# Revit family: CAF_DWDI_CW_UBD
name_source: partatom
category: Mechanical Equipment
units: mm (PartAtom-declared; Revit-internal decimal feet)

## family parameters
Always vertical = Yes
Cut with Voids When Loaded = No
Part Type = Normal
Room Calculation Point = No
Round Connector Dimension = Use Radius
Shared = No
Work Plane-Based = No

## types (58) — shared parameters
0 = 0"
1" = 1"
1.5 = 1 1/2"
2" = 2"
2' = 24"
3" = 3"
60 = 60.00°
Manufacturer = Loren Cook Company
Model = CAF-DWDI
ONE EIGTH = 1/8"
URL = www.lorencook.com

## per-type parameters (varying)
- 120_CAF-DWDI_CW_UBD_CLASS_1: ((M+U+U+N+N)-((B+.25")/2))/2=3"; (A+.25")/2=6 3/16"; (B+.25")/2=8 31/32"; (D-(A+.25"))/2=15/16"; (INLET/2)+1.5"=9 1/2"; (INLET/2)+1.625"=9 9/16"; (INLET/2)-.125"=7 15/16"; (M-(B+.25")/2=1 7/16"; -(B+.25")/2=-8 31/32"; -P=-26 11/16"; A=12 1/8"; A+.25"=12 3/8"; A/2=6 1/16"; B=17 11/16"; B+.25"=17 15/16"; B/2=8 27/32"; BOTTOM=9 5/8"; C=1 7/16"; C+C=2 7/8"; C/2=23/32"; D=14 1/4"; D/2=7 1/8"; D/7=1 1/2"; E=19 13/16"; E/2=9 29/32"; F=21 1/16"; F-((D-A-.25")/2)=20 1/8"; G=11 7/16"; G+(INLET/2)+1.625"=21"; G-(INLET/2)-1.625"=1 7/8"; G-(R/2)=1 13/16"; H=23 1/16"; H-((D-A-.25")/2)=22 1/8"; H-J=13 13/16"; INLET=16 1/8"; INLET/2=8 1/16"; INLET/4=4 1/32"; J=9 1/4"; K=9/16"; K/2=9/32"; L=10 7/16"; M=20 13/16"; N=2 3/4"; P=26 11/16"; R=19 1/4"; R/2=9 5/8"; S=14 7/8"; S/2=7 7/16"; SCROLL2=9"; T=19 7/16"; T/2=9 23/32"; Type Comments=Centrifugal Airfoil Blower Clockwise Up Blast Arrangement 3 Low Profile Class 1; U=4 5/16"; U-N=1 9/16"; V=1"; V+(D-(A+.25"))/2=1 15/16"
- 135_CAF-DWDI_CW_UBD_CLASS_1: ((M+U+U+N+N)-((B+.25")/2))/2=3"; (A+.25")/2=6 15/16"; (B+.25")/2=10 3/32"; (D-(A+.25"))/2=15/16"; (INLET/2)+1.5"=10 1/4"; (INLET/2)+1.625"=10 5/16"; (INLET/2)-.125"=8 11/16"; (M-(B+.25")/2=1 7/16"; -(B+.25")/2=-10 3/32"; -P=-28 15/16"; A=13 5/8"; A+.25"=13 7/8"; A/2=6 13/16"; B=19 15/16"; B+.25"=20 3/16"; B/2=9 31/32"; BOTTOM=10 13/16"; C=1 7/16"; C+C=2 7/8"; C/2=23/32"; D=15 3/4"; D/2=7 7/8"; D/7=1 21/32"; E=22 1/16"; E/2=11 1/32"; F=23 9/16"; F-((D-A-.25")/2)=22 5/8"; G=12 3/4"; G+(INLET/2)+1.625"=23 1/16"; G-(INLET/2)-1.625"=2 7/16"; G-(R/2)=2 1/4"; H=25 3/4"; H-((D-A-.25")/2)=24 13/16"; H-J=15 3/8"; INLET=17 5/8"; INLET/2=8 13/16"; INLET/4=4 13/32"; J=10 3/8"; K=9/16"; K/2=9/32"; L=11 9/16"; M=23 1/16"; N=2 3/4"; P=28 15/16"; R=21"; R/2=10 1/2"; S=16 5/8"; S/2=8 5/16"; SCROLL2=10 1/2"; T=21 3/4"; T/2=10 7/8"; Type Comments=Centrifugal Airfoil Blower Clockwise Up Blast Arrangement 3 Low Profile Class 1; U=4 5/16"; U-N=1 9/16"; V=1"; V+(D-(A+.25"))/2=1 15/16"
- 150_CAF-DWDI_CW_UBD_CLASS_1: ((M+U+U+N+N)-((B+.25")/2))/2=3"; (A+.25")/2=7 3/4"; (B+.25")/2=11 1/8"; (D-(A+.25"))/2=15/16"; (INLET/2)+1.5"=11"; (INLET/2)+1.625"=11 1/16"; (INLET/2)-.125"=9 7/16"; (M-(B+.25")/2=1 15/16"; -(B+.25")/2=-11 1/8"; -P=-31 5/8"; A=15 1/4"; A+.25"=15 1/2"; A/2=7 5/8"; B=22"; B+.25"=22 1/4"; B/2=11"; BOTTOM=12"; C=1 7/16"; C+C=2 7/8"; C/2=23/32"; D=17 3/8"; D/2=8 11/16"; D/7=1 27/32"; E=24 1/8"; E/2=12 1/16"; F=26 1/16"; F-((D-A-.25")/2)=25 1/8"; G=14 1/16"; G+(INLET/2)+1.625"=25 1/8"; G-(INLET/2)-1.625"=3"; G-(R/2)=2 13/16"; H=28 7/16"; H-((D-A-.25")/2)=27 1/2"; H-J=16 15/16"; INLET=19 1/8"; INLET/2=9 9/16"; INLET/4=4 25/32"; J=11 1/2"; K=9/16"; K/2=9/32"; L=13 1/16"; M=26 1/8"; N=3 3/8"; P=31 5/8"; R=22 1/2"; R/2=11 1/4"; S=17 3/4"; S/2=8 7/8"; SCROLL2=11 1/4"; T=24 3/8"; T/2=12 3/16"; Type Comments=Centrifugal Airfoil Blower Clockwise Up Blast Arrangement 3 Low Profile Class 1; U=4 7/16"; U-N=1 1/16"; V=1"; V+(D-(A+.25"))/2=1 15/16"
- 165_CAF-DWDI_CW_UBD_CLASS_1: ((M+U+U+N+N)-((B+.25")/2))/2=3"; (A+.25")/2=8 19/32"; (B+.25")/2=12 1/8"; (D-(A+.25"))/2=15/16"; (INLET/2)+1.5"=12 1/32"; (INLET/2)+1.625"=12 3/32"; (INLET/2)-.125"=10 15/32"; (M-(B+.25")/2=1 15/16"; -(B+.25")/2=-12 1/8"; -P=-33 11/16"; A=16 15/16"; A+.25"=17 3/16"; A/2=8 15/32"; B=24"; B+.25"=24 1/4"; B/2=12"; BOTTOM=13 1/8"; C=1 11/16"; C+C=3 3/8"; C/2=27/32"; D=19 1/16"; D/2=9 17/32"; D/7=2"; E=26 1/8"; E/2=13 1/16"; F=28 1/2"; F-((D-A-.25")/2)=27 9/16"; G=15 3/8"; G+(INLET/2)+1.625"=27 15/32"; G-(INLET/2)-1.625"=3 9/32"; G-(R/2)=3 1/4"; H=31 3/16"; H-((D-A-.25")/2)=30 1/4"; H-J=18 1/2"; INLET=21 3/16"; INLET/2=10 19/32"; INLET/4=5 5/16"; J=12 11/16"; K=15/16"; K/2=15/32"; L=14 1/16"; M=28 1/8"; N=3 3/8"; P=33 11/16"; R=24 1/4"; R/2=12 1/8"; S=19 1/2"; S/2=9 3/4"; SCROLL2=12 1/8"; T=26 3/8"; T/2=13 3/16"; Type Comments=Centrifugal Airfoil Blower Clockwise Up Blast Arrangement 3 Low Profile Class 1; U=4 7/16"; U-N=1 1/16"; V=1"; V+(D-(A+.25"))/2=1 15/16"
- 180_CAF-DWDI_CW_UBD_CLASS_1: ((M+U+U+N+N)-((B+.25")/2))/2=3"; (A+.25")/2=9 3/8"; (B+.25")/2=13 5/32"; (D-(A+.25"))/2=15/16"; (INLET/2)+1.5"=12 25/32"; (INLET/2)+1.625"=12 27/32"; (INLET/2)-.125"=11 7/32"; (M-(B+.25")/2=1 15/16"; -(B+.25")/2=-13 5/32"; -P=-36 1/8"; A=18 1/2"; A+.25"=18 3/4"; A/2=9 1/4"; B=26 1/16"; B+.25"=26 5/16"; B/2=13 1/32"; BOTTOM=14 5/16"; C=1 11/16"; C+C=3 3/8"; C/2=27/32"; D=20 5/8"; D/2=10 5/16"; D/7=2 5/32"; E=28 3/16"; E/2=14 3/32"; F=31"; F-((D-A-.25")/2)=30 1/16"; G=16 11/16"; G+(INLET/2)+1.625"=29 17/32"; G-(INLET/2)-1.625"=3 27/32"; G-(R/2)=3 5/16"; H=34"; H-((D-A-.25")/2)=33 1/16"; H-J=20 3/16"; INLET=22 11/16"; INLET/2=11 11/32"; INLET/4=5 11/16"; J=13 13/16"; K=15/16"; K/2=15/32"; L=15 1/8"; M=30 3/16"; N=3 3/4"; P=36 1/8"; R=26 3/4"; R/2=13 3/8"; S=21"; S/2=10 1/2"; SCROLL2=13 3/8"; T=28 7/16"; T/2=14 7/32"; Type Comments=Centrifugal Airfoil Blower Clockwise Up Blast Arrangement 3 Low Profile Class 1; U=4 13/16"; U-N=1 1/16"; V=1"; V+(D-(A+.25"))/2=1 15/16"
- 195_CAF-DWDI_CW_UBD_CLASS_1: ((M+U+U+N+N)-((B+.25")/2))/2=3"; (A+.25")/2=9 7/8"; (B+.25")/2=14 11/32"; (D-(A+.25"))/2=31/32"; (INLET/2)+1.5"=13 17/32"; (INLET/2)+1.625"=13 19/32"; (INLET/2)-.125"=11 31/32"; (M-(B+.25")/2=1 15/16"; -(B+.25")/2=-14 11/32"; -P=-38 1/2"; A=19 1/2"; A+.25"=19 3/4"; A/2=9 3/4"; B=28 7/16"; B+.25"=28 11/16"; B/2=14 7/32"; BOTTOM=15 1/2"; C=1 11/16"; C+C=3 3/8"; C/2=27/32"; D=21 11/16"; D/2=10 27/32"; D/7=2 9/32"; E=30 5/8"; E/2=15 5/16"; F=33 7/16"; F-((D-A-.25")/2)=32 15/32"; G=17 15/16"; G+(INLET/2)+1.625"=31 17/32"; G-(INLET/2)-1.625"=4 11/32"; G-(R/2)=3 11/16"; H=36 11/16"; H-((D-A-.25")/2)=35 23/32"; H-J=21 3/4"; INLET=24 3/16"; INLET/2=12 3/32"; INLET/4=6 1/16"; J=14 15/16"; K=15/16"; K/2=15/32"; L=16 5/16"; M=32 9/16"; N=3 3/4"; P=38 1/2"; R=28 1/2"; R/2=14 1/4"; S=22 3/4"; S/2=11 3/8"; SCROLL2=14 1/4"; T=30 13/16"; T/2=15 13/32"; Type Comments=Centrifugal Airfoil Blower Clockwise Up Blast Arrangement 3 Low Profile Class 1; U=4 13/16"; U-N=1 1/16"; V=1"; V+(D-(A+.25"))/2=1 31/32"
- 210_CAF-DWDI_CW_UBD_CLASS_1: ((M+U+U+N+N)-((B+.25")/2))/2=4"; (A+.25")/2=10 15/16"; (B+.25")/2=15 5/16"; (D-(A+.25"))/2=31/32"; (INLET/2)+1.5"=14 13/32"; (INLET/2)+1.625"=14 15/32"; (INLET/2)-.125"=12 27/32"; (M-(B+.25")/2=1 15/16"; -(B+.25")/2=-15 5/16"; -P=-41 7/16"; A=21 5/8"; A+.25"=21 7/8"; A/2=10 13/16"; B=30 3/8"; B+.25"=30 5/8"; B/2=15 3/16"; BOTTOM=16 11/16"; C=1 11/16"; C+C=3 3/8"; C/2=27/32"; D=23 13/16"; D/2=11 29/32"; D/7=2 1/2"; E=32 9/16"; E/2=16 9/32"; F=35 15/16"; F-((D-A-.25")/2)=34 31/32"; G=19 1/4"; G+(INLET/2)+1.625"=33 23/32"; G-(INLET/2)-1.625"=4 25/32"; G-(R/2)=4 1/4"; H=39 7/16"; H-((D-A-.25")/2)=38 15/32"; H-J=23 5/16"; INLET=25 15/16"; INLET/2=12 31/32"; INLET/4=6 1/2"; J=16 1/8"; K=15/16"; K/2=15/32"; L=17 1/4"; M=34 1/2"; N=3 3/4"; P=41 7/16"; R=30"; R/2=15"; S=24 1/4"; S/2=12 1/8"; SCROLL2=15"; T=32 3/4"; T/2=16 3/8"; Type Comments=Centrifugal Airfoil Blower Clockwise Up Blast Arrangement 3 Low Profile Class 1; U=5 13/16"; U-N=2 1/16"; V=1"; V+(D-(A+.25"))/2=1 31/32"
- 225_CAF-DWDI_CW_UBD_CLASS_1: ((M+U+U+N+N)-((B+.25")/2))/2=4"; (A+.25")/2=11 23/32"; (B+.25")/2=16 3/8"; (D-(A+.25"))/2=1 15/32"; (INLET/2)+1.5"=15 5/32"; (INLET/2)+1.625"=15 7/32"; (INLET/2)-.125"=13 19/32"; (M-(B+.25")/2=1 15/16"; -(B+.25")/2=-16 3/8"; -P=-44 1/16"; A=23 3/16"; A+.25"=23 7/16"; A/2=11 19/32"; B=32 1/2"; B+.25"=32 3/4"; B/2=16 1/4"; BOTTOM=17 13/16"; C=1 15/16"; C+C=3 7/8"; C/2=31/32"; D=26 3/8"; D/2=13 3/16"; D/7=2 25/32"; E=35 11/16"; E/2=17 27/32"; F=38 3/8"; F-((D-A-.25")/2)=36 29/32"; G=20 9/16"; G+(INLET/2)+1.625"=35 25/32"; G-(INLET/2)-1.625"=5 11/32"; G-(R/2)=4 11/16"; H=42 11/16"; H-((D-A-.25")/2)=41 7/32"; H-J=25 7/16"; INLET=27 7/16"; INLET/2=13 23/32"; INLET/4=6 7/8"; J=17 1/4"; K=15/16"; K/2=15/32"; L=18 5/16"; M=36 5/8"; N=4 1/4"; P=44 1/16"; R=31 3/4"; R/2=15 7/8"; S=26"; S/2=13"; SCROLL2=15 7/8"; T=34 7/8"; T/2=17 7/16"; Type Comments=Centrifugal Airfoil Blower Clockwise Up Blast Arrangement 3 Low Profile Class 1; U=6 5/16"; U-N=2 1/16"; V=1"; V+(D-(A+.25"))/2=2 15/32"
- 245_CAF-DWDI_CW_UBD_CLASS_1: ((M+U+U+N+N)-((B+.25")/2))/2=4"; (A+.25")/2=12 7/8"; (B+.25")/2=17 21/32"; (D-(A+.25"))/2=1 15/32"; (INLET/2)+1.5"=16 5/32"; (INLET/2)+1.625"=16 7/32"; (INLET/2)-.125"=14 19/32"; (M-(B+.25")/2=1 15/16"; -(B+.25")/2=-17 21/32"; -P=-46 5/8"; A=25 1/2"; A+.25"=25 3/4"; A/2=12 3/4"; B=35 1/16"; B+.25"=35 5/16"; B/2=17 17/32"; BOTTOM=19 3/8"; C=1 15/16"; C+C=3 7/8"; C/2=31/32"; D=28 11/16"; D/2=14 11/32"; D/7=3 1/32"; E=38 1/4"; E/2=19 1/8"; F=41 11/16"; F-((D-A-.25")/2)=40 7/32"; G=22 5/16"; G+(INLET/2)+1.625"=38 17/32"; G-(INLET/2)-1.625"=6 3/32"; G-(R/2)=5 7/16"; H=46 5/16"; H-((D-A-.25")/2)=44 27/32"; H-J=27 9/16"; INLET=29 7/16"; INLET/2=14 23/32"; INLET/4=7 3/8"; J=18 3/4"; K=15/16"; K/2=15/32"; L=19 5/8"; M=39 3/16"; N=4 1/4"; P=46 5/8"; R=33 3/4"; R/2=16 7/8"; S=28"; S/2=14"; SCROLL2=16 7/8"; T=37 7/16"; T/2=18 23/32"; Type Comments=Centrifugal Airfoil Blower Clockwise Up Blast Arrangement 3 Low Profile Class 1; U=6 5/16"; U-N=2 1/16"; V=1"; V+(D-(A+.25"))/2=2 15/32"
- 270_CAF-DWDI_CW_UBD_CLASS_1: ((M+U+U+N+N)-((B+.25")/2))/2=4 1/2"; (A+.25")/2=13 7/8"; (B+.25")/2=19 27/32"; (D-(A+.25"))/2=1 15/32"; (INLET/2)+1.5"=17 13/32"; (INLET/2)+1.625"=17 15/32"; (INLET/2)-.125"=15 27/32"; (M-(B+.25")/2=2 7/16"; -(B+.25")/2=-19 27/32"; -P=-51 1/2"; A=27 1/2"; A+.25"=27 3/4"; A/2=13 3/4"; B=39 7/16"; B+.25"=39 11/16"; B/2=19 23/32"; BOTTOM=21 5/16"; C=2 3/16"; C+C=4 3/8"; C/2=1 3/32"; D=30 11/16"; D/2=15 11/32"; D/7=3 7/32"; E=42 5/8"; E/2=21 5/16"; F=45 13/16"; F-((D-A-.25")/2)=44 11/32"; G=24 1/2"; G+(INLET/2)+1.625"=41 31/32"; G-(INLET/2)-1.625"=7 1/32"; G-(R/2)=5 3/4"; H=50 7/8"; H-((D-A-.25")/2)=49 13/32"; H-J=30 3/16"; INLET=31 15/16"; INLET/2=15 31/32"; INLET/4=8"; J=20 11/16"; K=15/16"; K/2=15/32"; L=22 5/16"; M=44 9/16"; N=4 1/4"; P=51 1/2"; R=37 1/2"; R/2=18 3/4"; S=30 1/4"; S/2=15 1/8"; SCROLL2=18 3/4"; T=42 5/16"; T/2=21 5/32"; Type Comments=Centrifugal Airfoil Blower Clockwise Up Blast Arrangement 3 Low Profile Class 1; U=6 5/16"; U-N=2 1/16"; V=1"; V+(D-(A+.25"))/2=2 15/32"
- 300_CAF-DWDI_CW_UBD_CLASS_1: ((M+U+U+N+N)-((B+.25")/2))/2=4 9/16"; (A+.25")/2=15 23/32"; (B+.25")/2=21 5/8"; (D-(A+.25"))/2=1 15/32"; (INLET/2)+1.5"=18 29/32"; (INLET/2)+1.625"=18 31/32"; (INLET/2)-.125"=17 11/32"; (M-(B+.25")/2=2 7/16"; -(B+.25")/2=-21 5/8"; -P=-55 1/8"; A=31 3/16"; A+.25"=31 7/16"; A/2=15 19/32"; B=43"; B+.25"=43 1/4"; B/2=21 1/2"; BOTTOM=23 11/16"; C=2 3/16"; C+C=4 3/8"; C/2=1 3/32"; D=34 3/8"; D/2=17 3/16"; D/7=3 5/8"; E=46 3/16"; E/2=23 3/32"; F=50 3/4"; F-((D-A-.25")/2)=49 9/32"; G=27 1/16"; G+(INLET/2)+1.625"=46 1/32"; G-(INLET/2)-1.625"=8 3/32"; G-(R/2)=6 13/16"; H=56 5/16"; H-((D-A-.25")/2)=54 27/32"; H-J=33 3/8"; INLET=34 15/16"; INLET/2=17 15/32"; INLET/4=8 3/4"; J=22 15/16"; K=15/16"; K/2=15/32"; L=24 1/16"; M=48 1/8"; N=4 1/4"; P=55 1/8"; R=40 1/2"; R/2=20 1/4"; S=33 1/4"; S/2=16 5/8"; SCROLL2=20 1/4"; T=45 7/8"; T/2=22 15/16"; Type Comments=Centrifugal Airfoil Blower Clockwise Up Blast Arrangement 3 Low Profile Class 1; U=6 3/8"; U-N=2 1/8"; V=1"; V+(D-(A+.25"))/2=2 15/32"
- 330_CAF-DWDI_CW_UBD_CLASS_1: ((M+U+U+N+N)-((B+.25")/2))/2=4 9/16"; (A+.25")/2=17 3/8"; (B+.25")/2=23 21/32"; (D-(A+.25"))/2=2"; (INLET/2)+1.5"=20 13/32"; (INLET/2)+1.625"=20 15/32"; (INLET/2)-.125"=18 27/32"; (M-(B+.25")/2=2 15/16"; -(B+.25")/2=-23 21/32"; -P=-59 5/16"; A=34 1/2"; A+.25"=34 3/4"; A/2=17 1/4"; B=47 1/16"; B+.25"=47 5/16"; B/2=23 17/32"; BOTTOM=26"; C=2 7/16"; C+C=4 7/8"; C/2=1 7/32"; D=38 3/4"; D/2=19 3/8"; D/7=4 3/32"; E=51 5/16"; E/2=25 21/32"; F=55 11/16"; F-((D-A-.25")/2)=53 11/16"; G=29 11/16"; G+(INLET/2)+1.625"=50 5/32"; G-(INLET/2)-1.625"=9 7/32"; G-(R/2)=8 29/32"; H=62 5/16"; H-((D-A-.25")/2)=60 5/16"; H-J=37 1/16"; INLET=37 15/16"; INLET/2=18 31/32"; INLET/4=9 1/2"; J=25 1/4"; K=15/16"; K/2=15/32"; L=26 5/8"; M=53 3/16"; N=4 3/8"; P=59 5/16"; R=41 9/16"; R/2=20 25/32"; S=36 1/8"; S/2=18 1/16"; SCROLL2=20 25/32"; T=50 9/16"; T/2=25 9/32"; Type Comments=Centrifugal Airfoil Blower Clockwise Up Blast Arrangement 3 Low Profile Class 1; U=6"; U-N=1 5/8"; V=1"; V+(D-(A+.25"))/2=3"
- 365_CAF-DWDI_CW_UBD_CLASS_1: ((M+U+U+N+N)-((B+.25")/2))/2=5 1/16"; (A+.25")/2=19 15/32"; (B+.25")/2=26 7/32"; (D-(A+.25"))/2=2"; (INLET/2)+1.5"=22 5/32"; (INLET/2)+1.625"=22 7/32"; (INLET/2)-.125"=20 19/32"; (M-(B+.25")/2=2 15/16"; -(B+.25")/2=-26 7/32"; -P=-65 5/16"; A=38 11/16"; A+.25"=38 15/16"; A/2=19 11/32"; B=52 3/16"; B+.25"=52 7/16"; B/2=26 3/32"; BOTTOM=28 3/4"; C=2 11/16"; C+C=5 3/8"; C/2=1 11/32"; D=42 15/16"; D/2=21 15/32"; D/7=4 17/32"; E=56 7/16"; E/2=28 7/32"; F=61 1/2"; F-((D-A-.25")/2)=59 1/2"; G=32 3/4"; G+(INLET/2)+1.625"=54 31/32"; G-(INLET/2)-1.625"=10 17/32"; G-(R/2)=10 3/32"; H=68 11/16"; H-((D-A-.25")/2)=66 11/16"; H-J=40 3/4"; INLET=41 7/16"; INLET/2=20 23/32"; INLET/4=10 3/8"; J=27 15/16"; K=15/16"; K/2=15/32"; L=29 3/16"; M=58 5/16"; N=4 3/4"; P=65 5/16"; R=45 5/16"; R/2=22 21/32"; S=39 7/8"; S/2=19 15/16"; SCROLL2=22 21/32"; T=55 11/16"; T/2=27 27/32"; Type Comments=Centrifugal Airfoil Blower Clockwise Up Blast Arrangement 3 Low Profile Class 1; U=6 7/8"; U-N=2 1/8"; V=1"; V+(D-(A+.25"))/2=3"
- 402_CAF-DWDI_CW_UBD_CLASS_1: ((M+U+U+N+N)-((B+.25")/2))/2=5 1/16"; (A+.25")/2=21"; (B+.25")/2=29 1/32"; (D-(A+.25"))/2=2 1/32"; (INLET/2)+1.5"=24 1/32"; (INLET/2)+1.625"=24 3/32"; (INLET/2)-.125"=22 15/32"; (M-(B+.25")/2=3 15/16"; -(B+.25")/2=-29 1/32"; -P=-71 15/16"; A=41 3/4"; A+.25"=42"; A/2=20 7/8"; B=57 13/16"; B+.25"=58 1/16"; B/2=28 29/32"; BOTTOM=31 11/16"; C=2 15/16"; C+C=5 7/8"; C/2=1 15/32"; D=46 1/16"; D/2=23 1/32"; D/7=4 27/32"; E=62"; E/2=31"; F=67 5/8"; F-((D-A-.25")/2)=65 19/32"; G=35 15/16"; G+(INLET/2)+1.625"=60 1/32"; G-(INLET/2)-1.625"=11 27/32"; G-(R/2)=11 3/32"; H=75 7/16"; H-((D-A-.25")/2)=73 13/32"; H-J=44 11/16"; INLET=45 3/16"; INLET/2=22 19/32"; INLET/4=11 5/16"; J=30 3/4"; K=15/16"; K/2=15/32"; L=33"; M=65 15/16"; N=4 7/8"; P=71 15/16"; R=49 11/16"; R/2=24 27/32"; S=43"; S/2=21 1/2"; SCROLL2=24 27/32"; T=62 7/16"; T/2=31 7/32"; Type Comments=Centrifugal Airfoil Blower Clockwise Up Blast Arrangement 3 Low Profile Class 1; U=6"; U-N=1 1/8"; V=1 15/16"; V+(D-(A+.25"))/2=3 31/32"
- 445_CAF-DWDI_CW_UBD_CLASS_1: ((M+U+U+N+N)-((B+.25")/2))/2=5 3/32"; (A+.25")/2=23 3/32"; (B+.25")/2=32 1/4"; (D-(A+.25"))/2=2 1/16"; (INLET/2)+1.5"=26 5/32"; (INLET/2)+1.625"=26 7/32"; (INLET/2)-.125"=24 19/32"; (M-(B+.25")/2=3 31/32"; -(B+.25")/2=-32 1/4"; -P=-79 5/16"; A=45 15/16"; A+.25"=46 3/16"; A/2=22 31/32"; B=64 1/4"; B+.25"=64 1/2"; B/2=32 1/8"; BOTTOM=35"; C=2 15/16"; C+C=5 7/8"; C/2=1 15/32"; D=50 5/16"; D/2=25 5/32"; D/7=5 9/32"; E=68 9/16"; E/2=34 9/32"; F=74 11/16"; F-((D-A-.25")/2)=72 5/8"; G=39 11/16"; G+(INLET/2)+1.625"=65 29/32"; G-(INLET/2)-1.625"=13 15/32"; G-(R/2)=12 23/32"; H=83 5/16"; H-((D-A-.25")/2)=81 1/4"; H-J=49 1/4"; INLET=49 7/16"; INLET/2=24 23/32"; INLET/4=12 3/8"; J=34 1/16"; K=1 1/16"; K/2=17/32"; L=36 1/4"; M=72 7/16"; N=5 3/4"; P=79 5/16"; R=53 15/16"; R/2=26 31/32"; S=47 1/4"; S/2=23 5/8"; SCROLL2=26 31/32"; T=68 15/16"; T/2=34 15/32"; Type Comments=Centrifugal Airfoil Blower Clockwise Up Blast Arrangement 3 Low Profile Class 1; U=6 7/8"; U-N=1 1/8"; V=1 15/16"; V+(D-(A+.25"))/2=4"
- 490_CAF-DWDI_CW_UBD_CLASS_1: ((M+U+U+N+N)-((B+.25")/2))/2=5 3/32"; (A+.25")/2=25 5/8"; (B+.25")/2=35 3/16"; (D-(A+.25"))/2=2 1/16"; (INLET/2)+1.5"=28 15/16"; (INLET/2)+1.625"=29"; (INLET/2)-.125"=27 3/8"; (M-(B+.25")/2=3 31/32"; -(B+.25")/2=-35 3/16"; -P=-85 5/16"; A=51"; A+.25"=51 1/4"; A/2=25 1/2"; B=70 1/8"; B+.25"=70 3/8"; B/2=35 1/16"; BOTTOM=38 9/16"; C=3 7/16"; C+C=6 7/8"; C/2=1 23/32"; D=55 3/8"; D/2=27 11/16"; D/7=5 27/32"; E=74 7/16"; E/2=37 7/32"; F=82 1/8"; F-((D-A-.25")/2)=80 1/16"; G=43 9/16"; G+(INLET/2)+1.625"=72 9/16"; G-(INLET/2)-1.625"=14 9/16"; G-(R/2)=14 7/32"; H=91 1/2"; H-((D-A-.25")/2)=89 7/16"; H-J=54"; INLET=55"; INLET/2=27 1/2"; INLET/4=13 3/4"; J=37 1/2"; K=1 1/16"; K/2=17/32"; L=39 3/16"; M=78 5/16"; N=5 7/8"; P=85 5/16"; R=58 11/16"; R/2=29 11/32"; S=52"; S/2=26"; SCROLL2=29 11/32"; T=74 13/16"; T/2=37 13/32"; Type Comments=Centrifugal Airfoil Blower Clockwise Up Blast Arrangement 3 Low Profile Class 1; U=7"; U-N=1 1/8"; V=1 15/16"; V+(D-(A+.25"))/2=4"
- 540_CAF-DWDI_CW_UBD_CLASS_1: ((M+U+U+N+N)-((B+.25")/2))/2=5 3/32"; (A+.25")/2=28"; (B+.25")/2=39 3/32"; (D-(A+.25"))/2=2 1/16"; (INLET/2)+1.5"=31 7/16"; (INLET/2)+1.625"=31 1/2"; (INLET/2)-.125"=29 7/8"; (M-(B+.25")/2=3 31/32"; -(B+.25")/2=-39 3/32"; -P=-93 1/2"; A=55 3/4"; A+.25"=56"; A/2=27 7/8"; B=77 15/16"; B+.25"=78 3/16"; B/2=38 31/32"; BOTTOM=42 7/16"; C=2 15/16"; C+C=5 7/8"; C/2=1 15/32"; D=60 1/8"; D/2=30 1/16"; D/7=6 11/32"; E=82 3/16"; E/2=41 3/32"; F=90 3/8"; F-((D-A-.25")/2)=88 5/16"; G=47 15/16"; G+(INLET/2)+1.625"=79 7/16"; G-(INLET/2)-1.625"=16 7/16"; G-(R/2)=16 3/32"; H=100 5/8"; H-((D-A-.25")/2)=98 9/16"; H-J=59 5/16"; INLET=60"; INLET/2=30"; INLET/4=15"; J=41 5/16"; K=1 1/16"; K/2=17/32"; L=43 1/16"; M=86 1/8"; N=6 1/4"; P=93 1/2"; R=63 11/16"; R/2=31 27/32"; S=57"; S/2=28 1/2"; SCROLL2=31 27/32"; T=82 5/8"; T/2=41 5/16"; Type Comments=Centrifugal Airfoil Blower Clockwise Up Blast Arrangement 3 Low Profile Class 1; U=7 3/8"; U-N=1 1/8"; V=1 15/16"; V+(D-(A+.25"))/2=4"
- 600_CAF-DWDI_CW_UBD_CLASS_1: ((M+U+U+N+N)-((B+.25")/2))/2=5 1/8"; (A+.25")/2=31 7/32"; (B+.25")/2=43 1/4"; (D-(A+.25"))/2=2 1/16"; (INLET/2)+1.5"=34 7/16"; (INLET/2)+1.625"=34 1/2"; (INLET/2)-.125"=32 7/8"; (M-(B+.25")/2=5"; -(B+.25")/2=-43 1/4"; -P=-102 7/8"; A=62 3/16"; A+.25"=62 7/16"; A/2=31 3/32"; B=86 1/4"; B+.25"=86 1/2"; B/2=43 1/8"; BOTTOM=47 1/8"; C=2 15/16"; C+C=5 7/8"; C/2=1 15/32"; D=66 9/16"; D/2=33 9/32"; D/7=7"; E=90 9/16"; E/2=45 9/32"; F=100 5/16"; F-((D-A-.25")/2)=98 1/4"; G=53 3/16"; G+(INLET/2)+1.625"=87 11/16"; G-(INLET/2)-1.625"=18 11/16"; G-(R/2)=18 3/16"; H=111 5/8"; H-((D-A-.25")/2)=109 9/16"; H-J=65 11/16"; INLET=66"; INLET/2=33"; INLET/4=16 1/2"; J=45 15/16"; K=1 1/16"; K/2=17/32"; L=48 1/4"; M=96 1/2"; N=6 1/4"; P=102 7/8"; R=70"; R/2=35"; S=62"; S/2=31"; SCROLL2=35"; T=92"; T/2=46"; Type Comments=Centrifugal Airfoil Blower Clockwise Up Blast Arrangement 3 Low Profile Class 1; U=6 3/8"; U-N=1/8"; V=2 15/16"; V+(D-(A+.25"))/2=5"
- 660_CAF-DWDI_CW_UBD_CLASS_1: ((M+U+U+N+N)-((B+.25")/2))/2=6 5/8"; (A+.25")/2=34 11/32"; (B+.25")/2=47 9/16"; (D-(A+.25"))/2=2 1/16"; (INLET/2)+1.5"=37 7/16"; (INLET/2)+1.625"=37 1/2"; (INLET/2)-.125"=35 7/8"; (M-(B+.25")/2=6"; -(B+.25")/2=-47 9/16"; -P=-117 1/8"; A=68 7/16"; A+.25"=68 11/16"; A/2=34 7/32"; B=94 7/8"; B+.25"=95 1/8"; B/2=47 7/16"; BOTTOM=51 13/16"; C=3 7/16"; C+C=6 7/8"; C/2=1 23/32"; D=72 13/16"; D/2=36 13/32"; D/7=7 21/32"; E=99 1/4"; E/2=49 5/8"; F=110 3/16"; F-((D-A-.25")/2)=108 1/8"; G=58 3/8"; G+(INLET/2)+1.625"=95 7/8"; G-(INLET/2)-1.625"=20 7/8"; G-(R/2)=20 3/32"; H=122 9/16"; H-((D-A-.25")/2)=120 1/2"; H-J=72 1/16"; INLET=72"; INLET/2=36"; INLET/4=18"; J=50 1/2"; K=1 1/16"; K/2=17/32"; L=53 9/16"; M=107 1/8"; N=9 3/8"; P=117 1/8"; R=76 9/16"; R/2=38 9/32"; S=67"; S/2=33 1/2"; SCROLL2=38 9/32"; T=101 5/8"; T/2=50 13/16"; Type Comments=Centrifugal Airfoil Blower Clockwise Up Blast Arrangement 3 Low Profile Class 1; U=10"; U-N=5/8"; V=3 15/16"; V+(D-(A+.25"))/2=6"
- 730_CAF-DWDI_CW_UBD_CLASS_1: ((M+U+U+N+N)-((B+.25")/2))/2=6 5/8"; (A+.25")/2=38 1/32"; (B+.25")/2=52 1/2"; (D-(A+.25"))/2=2 9/16"; (INLET/2)+1.5"=40 15/16"; (INLET/2)+1.625"=41"; (INLET/2)-.125"=39 3/8"; (M-(B+.25")/2=6"; -(B+.25")/2=-52 1/2"; -P=-127"; A=75 13/16"; A+.25"=76 1/16"; A/2=37 29/32"; B=104 3/4"; B+.25"=105"; B/2=52 3/8"; BOTTOM=57 5/16"; C=3 7/16"; C+C=6 7/8"; C/2=1 23/32"; D=81 3/16"; D/2=40 19/32"; D/7=8 17/32"; E=110 1/8"; E/2=55 1/16"; F=121 3/4"; F-((D-A-.25")/2)=119 3/16"; G=64 7/16"; G+(INLET/2)+1.625"=105 7/16"; G-(INLET/2)-1.625"=23 7/16"; G-(R/2)=22 21/32"; H=135 13/16"; H-((D-A-.25")/2)=133 1/4"; H-J=80"; INLET=79"; INLET/2=39 1/2"; INLET/4=19 3/4"; J=55 13/16"; K=1 1/16"; K/2=17/32"; L=58 1/2"; M=117"; N=9 3/8"; P=127"; R=83 9/16"; R/2=41 25/32"; S=74"; S/2=37"; SCROLL2=41 25/32"; T=111 1/2"; T/2=55 3/4"; Type Comments=Centrifugal Airfoil Blower Clockwise Up Blast Arrangement 3 Low Profile Class 1; U=10"; U-N=5/8"; V=3 7/16"; V+(D-(A+.25"))/2=6"
- 120_CAF-DWDI_CW_UBD_CLASS_2: ((M+U+U+N+N)-((B+.25")/2))/2=3 1/2"; (A+.25")/2=6 3/16"; (B+.25")/2=8 31/32"; (D-(A+.25"))/2=15/16"; (INLET/2)+1.5"=9 1/2"; (INLET/2)+1.625"=9 9/16"; (INLET/2)-.125"=7 15/16"; (M-(B+.25")/2=1 15/16"; -(B+.25")/2=-8 31/32"; -P=-28 3/16"; A=12 1/8"; A+.25"=12 3/8"; A/2=6 1/16"; B=17 11/16"; B+.25"=17 15/16"; B/2=8 27/32"; BOTTOM=9 5/8"; C=1 7/16"; C+C=2 7/8"; C/2=23/32"; D=14 1/4"; D/2=7 1/8"; D/7=1 1/2"; E=19 13/16"; E/2=9 29/32"; F=21 1/16"; F-((D-A-.25")/2)=20 1/8"; G=11 7/16"; G+(INLET/2)+1.625"=21"; G-(INLET/2)-1.625"=1 7/8"; G-(R/2)=1 13/16"; H=23"; H-((D-A-.25")/2)=22 1/16"; H-J=13 3/4"; INLET=16 1/8"; INLET/2=8 1/16"; INLET/4=4 1/32"; J=9 1/4"; K=15/16"; K/2=15/32"; L=10 15/16"; M=21 13/16"; N=3 3/4"; P=28 3/16"; R=19 1/4"; R/2=9 5/8"; S=14 3/8"; S/2=7 3/16"; SCROLL2=9"; T=19 15/16"; T/2=9 31/32"; Type Comments=Centrifugal Airfoil Blower Clockwise Up Blast Arrangement 3 Low Profile Class 2; U=5 5/16"; U-N=1 9/16"; V=1"; V+(D-(A+.25"))/2=1 15/16"
- 135_CAF-DWDI_CW_UBD_CLASS_2: ((M+U+U+N+N)-((B+.25")/2))/2=3 1/2"; (A+.25")/2=6 15/16"; (B+.25")/2=10 3/32"; (D-(A+.25"))/2=15/16"; (INLET/2)+1.5"=10 1/4"; (INLET/2)+1.625"=10 5/16"; (INLET/2)-.125"=8 11/16"; (M-(B+.25")/2=1 15/16"; -(B+.25")/2=-10 3/32"; -P=-30 9/16"; A=13 5/8"; A+.25"=13 7/8"; A/2=6 13/16"; B=19 15/16"; B+.25"=20 3/16"; B/2=9 31/32"; BOTTOM=10 13/16"; C=1 7/16"; C+C=2 7/8"; C/2=23/32"; D=15 3/4"; D/2=7 7/8"; D/7=1 21/32"; E=22 1/16"; E/2=11 1/32"; F=23 9/16"; F-((D-A-.25")/2)=22 5/8"; G=12 3/4"; G+(INLET/2)+1.625"=23 1/16"; G-(INLET/2)-1.625"=2 7/16"; G-(R/2)=2 1/4"; H=25 3/4"; H-((D-A-.25")/2)=24 13/16"; H-J=15 3/8"; INLET=17 5/8"; INLET/2=8 13/16"; INLET/4=4 13/32"; J=10 3/8"; K=15/16"; K/2=15/32"; L=12 1/16"; M=24 1/16"; N=3 7/8"; P=30 9/16"; R=21"; R/2=10 1/2"; S=16 1/8"; S/2=8 1/16"; SCROLL2=10 1/2"; T=22 3/16"; T/2=11 3/32"; Type Comments=Centrifugal Airfoil Blower Clockwise Up Blast Arrangement 3 Low Profile Class 2; U=5 7/16"; U-N=1 9/16"; V=1"; V+(D-(A+.25"))/2=1 15/16"
- 150_CAF-DWDI_CW_UBD_CLASS_2: ((M+U+U+N+N)-((B+.25")/2))/2=4"; (A+.25")/2=7 3/4"; (B+.25")/2=11 1/8"; (D-(A+.25"))/2=15/16"; (INLET/2)+1.5"=11"; (INLET/2)+1.625"=11 1/16"; (INLET/2)-.125"=9 7/16"; (M-(B+.25")/2=1 15/16"; -(B+.25")/2=-11 1/8"; -P=-33 1/8"; A=15 1/4"; A+.25"=15 1/2"; A/2=7 5/8"; B=22"; B+.25"=22 1/4"; B/2=11"; BOTTOM=12"; C=1 15/16"; C+C=3 7/8"; C/2=31/32"; D=17 3/8"; D/2=8 11/16"; D/7=1 27/32"; E=24 1/8"; E/2=12 1/16"; F=26 1/16"; F-((D-A-.25")/2)=25 1/8"; G=14 1/16"; G+(INLET/2)+1.625"=25 1/8"; G-(INLET/2)-1.625"=3"; G-(R/2)=2 5/16"; H=28 7/16"; H-((D-A-.25")/2)=27 1/2"; H-J=16 15/16"; INLET=19 1/8"; INLET/2=9 9/16"; INLET/4=4 25/32"; J=11 1/2"; K=15/16"; K/2=15/32"; L=13 1/16"; M=26 1/8"; N=3 7/8"; P=33 1/8"; R=23 1/2"; R/2=11 3/4"; S=17 3/4"; S/2=8 7/8"; SCROLL2=11 1/4"; T=24 3/8"; T/2=12 3/16"; Type Comments=Centrifugal Airfoil Blower Clockwise Up Blast Arrangement 3 Low Profile Class 2; U=5 15/16"; U-N=2 1/16"; V=1"; V+(D-(A+.25"))/2=1 15/16"
- 165_CAF-DWDI_CW_UBD_CLASS_2: ((M+U+U+N+N)-((B+.25")/2))/2=4"; (A+.25")/2=8 19/32"; (B+.25")/2=12 1/8"; (D-(A+.25"))/2=15/16"; (INLET/2)+1.5"=12 1/32"; (INLET/2)+1.625"=12 3/32"; (INLET/2)-.125"=10 15/32"; (M-(B+.25")/2=1 15/16"; -(B+.25")/2=-12 1/8"; -P=-35 3/16"; A=16 15/16"; A+.25"=17 3/16"; A/2=8 15/32"; B=24"; B+.25"=24 1/4"; B/2=12"; BOTTOM=13 1/8"; C=1 15/16"; C+C=3 7/8"; C/2=31/32"; D=19 1/16"; D/2=9 17/32"; D/7=2"; E=26 1/8"; E/2=13 1/16"; F=28 1/2"; F-((D-A-.25")/2)=27 9/16"; G=15 3/8"; G+(INLET/2)+1.625"=27 15/32"; G-(INLET/2)-1.625"=3 9/32"; G-(R/2)=2 3/4"; H=31 3/16"; H-((D-A-.25")/2)=30 1/4"; H-J=18 1/2"; INLET=21 3/16"; INLET/2=10 19/32"; INLET/4=5 5/16"; J=12 11/16"; K=15/16"; K/2=15/32"; L=14 1/16"; M=28 1/8"; N=3 7/8"; P=35 3/16"; R=25 1/4"; R/2=12 5/8"; S=19 1/2"; S/2=9 3/4"; SCROLL2=12 1/8"; T=26 3/8"; T/2=13 3/16"; Type Comments=Centrifugal Airfoil Blower Clockwise Up Blast Arrangement 3 Low Profile Class 2; U=5 15/16"; U-N=2 1/16"; V=1"; V+(D-(A+.25"))/2=1 15/16"
- 180_CAF-DWDI_CW_UBD_CLASS_2: ((M+U+U+N+N)-((B+.25")/2))/2=4"; (A+.25")/2=9 3/8"; (B+.25")/2=13 5/32"; (D-(A+.25"))/2=1"; (INLET/2)+1.5"=12 25/32"; (INLET/2)+1.625"=12 27/32"; (INLET/2)-.125"=11 7/32"; (M-(B+.25")/2=1 15/16"; -(B+.25")/2=-13 5/32"; -P=-37 1/4"; A=18 1/2"; A+.25"=18 3/4"; A/2=9 1/4"; B=26 1/16"; B+.25"=26 5/16"; B/2=13 1/32"; BOTTOM=14 5/16"; C=1 15/16"; C+C=3 7/8"; C/2=31/32"; D=20 3/4"; D/2=10 3/8"; D/7=2 3/16"; E=28 3/16"; E/2=14 3/32"; F=31"; F-((D-A-.25")/2)=30"; G=16 11/16"; G+(INLET/2)+1.625"=29 17/32"; G-(INLET/2)-1.625"=3 27/32"; G-(R/2)=3 5/16"; H=34"; H-((D-A-.25")/2)=33"; H-J=20 3/16"; INLET=22 11/16"; INLET/2=11 11/32"; INLET/4=5 11/16"; J=13 13/16"; K=15/16"; K/2=15/32"; L=15 1/8"; M=30 3/16"; N=3 7/8"; P=37 1/4"; R=26 3/4"; R/2=13 3/8"; S=21"; S/2=10 1/2"; SCROLL2=13 3/8"; T=28 7/16"; T/2=14 7/32"; Type Comments=Centrifugal Airfoil Blower Clockwise Up Blast Arrangement 3 Low Profile Class 2; U=5 15/16"; U-N=2 1/16"; V=1"; V+(D-(A+.25"))/2=2"
- 195_CAF-DWDI_CW_UBD_CLASS_2: ((M+U+U+N+N)-((B+.25")/2))/2=4"; (A+.25")/2=9 7/8"; (B+.25")/2=14 11/32"; (D-(A+.25"))/2=15/16"; (INLET/2)+1.5"=13 17/32"; (INLET/2)+1.625"=13 19/32"; (INLET/2)-.125"=11 31/32"; (M-(B+.25")/2=1 15/16"; -(B+.25")/2=-14 11/32"; -P=-39 5/8"; A=19 1/2"; A+.25"=19 3/4"; A/2=9 3/4"; B=28 7/16"; B+.25"=28 11/16"; B/2=14 7/32"; BOTTOM=15 1/2"; C=1 15/16"; C+C=3 7/8"; C/2=31/32"; D=21 5/8"; D/2=10 13/16"; D/7=2 9/32"; E=30 9/16"; E/2=15 9/32"; F=33 7/16"; F-((D-A-.25")/2)=32 1/2"; G=17 15/16"; G+(INLET/2)+1.625"=31 17/32"; G-(INLET/2)-1.625"=4 11/32"; G-(R/2)=3 11/16"; H=36 5/8"; H-((D-A-.25")/2)=35 11/16"; H-J=21 11/16"; INLET=24 3/16"; INLET/2=12 3/32"; INLET/4=6 1/16"; J=14 15/16"; K=15/16"; K/2=15/32"; L=16 5/16"; M=32 9/16"; N=3 7/8"; P=39 5/8"; R=28 1/2"; R/2=14 1/4"; S=22 3/4"; S/2=11 3/8"; SCROLL2=14 1/4"; T=30 13/16"; T/2=15 13/32"; Type Comments=Centrifugal Airfoil Blower Clockwise Up Blast Arrangement 3 Low Profile Class 2; U=5 15/16"; U-N=2 1/16"; V=1"; V+(D-(A+.25"))/2=1 15/16"
- 210_CAF-DWDI_CW_UBD_CLASS_2: ((M+U+U+N+N)-((B+.25")/2))/2=4 1/2"; (A+.25")/2=10 15/16"; (B+.25")/2=15 5/16"; (D-(A+.25"))/2=31/32"; (INLET/2)+1.5"=14 13/32"; (INLET/2)+1.625"=14 15/32"; (INLET/2)-.125"=12 27/32"; (M-(B+.25")/2=1 15/16"; -(B+.25")/2=-15 5/16"; -P=-42 7/16"; A=21 5/8"; A+.25"=21 7/8"; A/2=10 13/16"; B=30 3/8"; B+.25"=30 5/8"; B/2=15 3/16"; BOTTOM=16 11/16"; C=2 3/16"; C+C=4 3/8"; C/2=1 3/32"; D=23 13/16"; D/2=11 29/32"; D/7=2 1/2"; E=32 9/16"; E/2=16 9/32"; F=35 15/16"; F-((D-A-.25")/2)=34 31/32"; G=19 1/4"; G+(INLET/2)+1.625"=33 23/32"; G-(INLET/2)-1.625"=4 25/32"; G-(R/2)=4 1/4"; H=39 7/16"; H-((D-A-.25")/2)=38 15/32"; H-J=23 5/16"; INLET=25 15/16"; INLET/2=12 31/32"; INLET/4=6 1/2"; J=16 1/8"; K=15/16"; K/2=15/32"; L=17 1/4"; M=34 1/2"; N=4 1/4"; P=42 7/16"; R=30"; R/2=15"; S=24 1/4"; S/2=12 1/8"; SCROLL2=15"; T=32 3/4"; T/2=16 3/8"; Type Comments=Centrifugal Airfoil Blower Clockwise Up Blast Arrangement 3 Low Profile Class 2; U=6 13/16"; U-N=2 9/16"; V=1"; V+(D-(A+.25"))/2=1 31/32"
- 225_CAF-DWDI_CW_UBD_CLASS_2: ((M+U+U+N+N)-((B+.25")/2))/2=4 1/2"; (A+.25")/2=11 23/32"; (B+.25")/2=16 3/8"; (D-(A+.25"))/2=1 15/32"; (INLET/2)+1.5"=15 5/32"; (INLET/2)+1.625"=15 7/32"; (INLET/2)-.125"=13 19/32"; (M-(B+.25")/2=1 15/16"; -(B+.25")/2=-16 3/8"; -P=-44 9/16"; A=23 3/16"; A+.25"=23 7/16"; A/2=11 19/32"; B=32 1/2"; B+.25"=32 3/4"; B/2=16 1/4"; BOTTOM=17 13/16"; C=2 3/16"; C+C=4 3/8"; C/2=1 3/32"; D=26 3/8"; D/2=13 3/16"; D/7=2 25/32"; E=35 11/16"; E/2=17 27/32"; F=38 3/8"; F-((D-A-.25")/2)=36 29/32"; G=20 9/16"; G+(INLET/2)+1.625"=35 25/32"; G-(INLET/2)-1.625"=5 11/32"; G-(R/2)=4 11/16"; H=42 11/16"; H-((D-A-.25")/2)=41 7/32"; H-J=25 7/16"; INLET=27 7/16"; INLET/2=13 23/32"; INLET/4=6 7/8"; J=17 1/4"; K=15/16"; K/2=15/32"; L=18 5/16"; M=36 5/8"; N=4 1/4"; P=44 9/16"; R=31 3/4"; R/2=15 7/8"; S=26"; S/2=13"; SCROLL2=15 7/8"; T=34 7/8"; T/2=17 7/16"; Type Comments=Centrifugal Airfoil Blower Clockwise Up Blast Arrangement 3 Low Profile Class 2; U=6 13/16"; U-N=2 9/16"; V=1"; V+(D-(A+.25"))/2=2 15/32"
- 245_CAF-DWDI_CW_UBD_CLASS_2: ((M+U+U+N+N)-((B+.25")/2))/2=4 1/2"; (A+.25")/2=12 7/8"; (B+.25")/2=17 21/32"; (D-(A+.25"))/2=1 15/32"; (INLET/2)+1.5"=16 5/32"; (INLET/2)+1.625"=16 7/32"; (INLET/2)-.125"=14 19/32"; (M-(B+.25")/2=1 15/16"; -(B+.25")/2=-17 21/32"; -P=-47 1/4"; A=25 1/2"; A+.25"=25 3/4"; A/2=12 3/4"; B=35 1/16"; B+.25"=35 5/16"; B/2=17 17/32"; BOTTOM=19 3/8"; C=2 7/16"; C+C=4 7/8"; C/2=1 7/32"; D=28 11/16"; D/2=14 11/32"; D/7=3 1/32"; E=38 1/4"; E/2=19 1/8"; F=41 11/16"; F-((D-A-.25")/2)=40 7/32"; G=22 5/16"; G+(INLET/2)+1.625"=38 17/32"; G-(INLET/2)-1.625"=6 3/32"; G-(R/2)=5 7/16"; H=46 5/16"; H-((D-A-.25")/2)=44 27/32"; H-J=27 9/16"; INLET=29 7/16"; INLET/2=14 23/32"; INLET/4=7 3/8"; J=18 3/4"; K=15/16"; K/2=15/32"; L=19 5/8"; M=39 3/16"; N=4 3/8"; P=47 1/4"; R=33 3/4"; R/2=16 7/8"; S=28"; S/2=14"; SCROLL2=16 7/8"; T=37 7/16"; T/2=18 23/32"; Type Comments=Centrifugal Airfoil Blower Clockwise Up Blast Arrangement 3 Low Profile Class 2; U=6 15/16"; U-N=2 9/16"; V=1"; V+(D-(A+.25"))/2=2 15/32"
- 270_CAF-DWDI_CW_UBD_CLASS_2: ((M+U+U+N+N)-((B+.25")/2))/2=4 1/2"; (A+.25")/2=13 7/8"; (B+.25")/2=19 27/32"; (D-(A+.25"))/2=1 15/32"; (INLET/2)+1.5"=17 13/32"; (INLET/2)+1.625"=17 15/32"; (INLET/2)-.125"=15 27/32"; (M-(B+.25")/2=2 7/16"; -(B+.25")/2=-19 27/32"; -P=-51 5/8"; A=27 1/2"; A+.25"=27 3/4"; A/2=13 3/4"; B=39 7/16"; B+.25"=39 11/16"; B/2=19 23/32"; BOTTOM=21 5/16"; C=2 7/16"; C+C=4 7/8"; C/2=1 7/32"; D=30 11/16"; D/2=15 11/32"; D/7=3 7/32"; E=42 5/8"; E/2=21 5/16"; F=45 13/16"; F-((D-A-.25")/2)=44 11/32"; G=24 1/2"; G+(INLET/2)+1.625"=41 31/32"; G-(INLET/2)-1.625"=7 1/32"; G-(R/2)=5 3/4"; H=50 7/8"; H-((D-A-.25")/2)=49 13/32"; H-J=30 3/16"; INLET=31 15/16"; INLET/2=15 31/32"; INLET/4=8"; J=20 11/16"; K=15/16"; K/2=15/32"; L=22 5/16"; M=44 9/16"; N=4 3/8"; P=51 5/8"; R=37 1/2"; R/2=18 3/4"; S=30 1/4"; S/2=15 1/8"; SCROLL2=18 3/4"; T=42 5/16"; T/2=21 5/32"; Type Comments=Centrifugal Airfoil Blower Clockwise Up Blast Arrangement 3 Low Profile Class 2; U=6 7/16"; U-N=2 1/16"; V=1"; V+(D-(A+.25"))/2=2 15/32"
- 300_CAF-DWDI_CW_UBD_CLASS_2: ((M+U+U+N+N)-((B+.25")/2))/2=5 1/16"; (A+.25")/2=15 23/32"; (B+.25")/2=21 5/8"; (D-(A+.25"))/2=1 15/32"; (INLET/2)+1.5"=18 29/32"; (INLET/2)+1.625"=18 31/32"; (INLET/2)-.125"=17 11/32"; (M-(B+.25")/2=2 7/16"; -(B+.25")/2=-21 5/8"; -P=-56 1/8"; A=31 3/16"; A+.25"=31 7/16"; A/2=15 19/32"; B=43"; B+.25"=43 1/4"; B/2=21 1/2"; BOTTOM=23 11/16"; C=2 11/16"; C+C=5 3/8"; C/2=1 11/32"; D=34 3/8"; D/2=17 3/16"; D/7=3 5/8"; E=46 3/16"; E/2=23 3/32"; F=50 3/4"; F-((D-A-.25")/2)=49 9/32"; G=27 1/16"; G+(INLET/2)+1.625"=46 1/32"; G-(INLET/2)-1.625"=8 3/32"; G-(R/2)=6 13/16"; H=56 5/16"; H-((D-A-.25")/2)=54 27/32"; H-J=33 3/8"; INLET=34 15/16"; INLET/2=17 15/32"; INLET/4=8 3/4"; J=22 15/16"; K=1 1/16"; K/2=17/32"; L=24 1/16"; M=48 1/8"; N=4 3/4"; P=56 1/8"; R=40 1/2"; R/2=20 1/4"; S=33 1/4"; S/2=16 5/8"; SCROLL2=20 1/4"; T=45 7/8"; T/2=22 15/16"; Type Comments=Centrifugal Airfoil Blower Clockwise Up Blast Arrangement 3 Low Profile Class 2; U=7 3/8"; U-N=2 5/8"; V=1"; V+(D-(A+.25"))/2=2 15/32"
- 330_CAF-DWDI_CW_UBD_CLASS_2: ((M+U+U+N+N)-((B+.25")/2))/2=5 1/16"; (A+.25")/2=17 3/8"; (B+.25")/2=23 21/32"; (D-(A+.25"))/2=2"; (INLET/2)+1.5"=20 13/32"; (INLET/2)+1.625"=20 15/32"; (INLET/2)-.125"=18 27/32"; (M-(B+.25")/2=2 15/16"; -(B+.25")/2=-23 21/32"; -P=-60 5/16"; A=34 1/2"; A+.25"=34 3/4"; A/2=17 1/4"; B=47 1/16"; B+.25"=47 5/16"; B/2=23 17/32"; BOTTOM=26"; C=2 15/16"; C+C=5 7/8"; C/2=1 15/32"; D=38 3/4"; D/2=19 3/8"; D/7=4 3/32"; E=51 5/16"; E/2=25 21/32"; F=55 11/16"; F-((D-A-.25")/2)=53 11/16"; G=29 11/16"; G+(INLET/2)+1.625"=50 5/32"; G-(INLET/2)-1.625"=9 7/32"; G-(R/2)=8 15/16"; H=62 5/16"; H-((D-A-.25")/2)=60 5/16"; H-J=37 1/16"; INLET=37 15/16"; INLET/2=18 31/32"; INLET/4=9 1/2"; J=25 1/4"; K=1 1/16"; K/2=17/32"; L=26 5/8"; M=53 3/16"; N=4 7/8"; P=60 5/16"; R=41 1/2"; R/2=20 3/4"; S=36 1/8"; S/2=18 1/16"; SCROLL2=20 25/32"; T=50 9/16"; T/2=25 9/32"; Type Comments=Centrifugal Airfoil Blower Clockwise Up Blast Arrangement 3 Low Profile Class 2; U=7"; U-N=2 1/8"; V=1"; V+(D-(A+.25"))/2=3"
- 365_CAF-DWDI_CW_UBD_CLASS_2: ((M+U+U+N+N)-((B+.25")/2))/2=5 1/16"; (A+.25")/2=19 15/32"; (B+.25")/2=26 7/32"; (D-(A+.25"))/2=2"; (INLET/2)+1.5"=22 5/32"; (INLET/2)+1.625"=22 7/32"; (INLET/2)-.125"=20 19/32"; (M-(B+.25")/2=2 15/16"; -(B+.25")/2=-26 7/32"; -P=-65 5/16"; A=38 11/16"; A+.25"=38 15/16"; A/2=19 11/32"; B=52 3/16"; B+.25"=52 7/16"; B/2=26 3/32"; BOTTOM=28 3/4"; C=3 7/16"; C+C=6 7/8"; C/2=1 23/32"; D=42 15/16"; D/2=21 15/32"; D/7=4 17/32"; E=56 7/16"; E/2=28 7/32"; F=61 1/2"; F-((D-A-.25")/2)=59 1/2"; G=32 3/4"; G+(INLET/2)+1.625"=54 31/32"; G-(INLET/2)-1.625"=10 17/32"; G-(R/2)=10 1/8"; H=68 11/16"; H-((D-A-.25")/2)=66 11/16"; H-J=40 3/4"; INLET=41 7/16"; INLET/2=20 23/32"; INLET/4=10 3/8"; J=27 15/16"; K=1 1/16"; K/2=17/32"; L=29 3/16"; M=58 5/16"; N=5 3/8"; P=65 5/16"; R=45 1/4"; R/2=22 5/8"; S=39 7/8"; S/2=19 15/16"; SCROLL2=22 21/32"; T=55 11/16"; T/2=27 27/32"; Type Comments=Centrifugal Airfoil Blower Clockwise Up Blast Arrangement 3 Low Profile Class 2; U=7 1/2"; U-N=2 1/8"; V=1"; V+(D-(A+.25"))/2=3"
- 402_CAF-DWDI_CW_UBD_CLASS_2: ((M+U+U+N+N)-((B+.25")/2))/2=5 3/32"; (A+.25")/2=21"; (B+.25")/2=29 1/32"; (D-(A+.25"))/2=2 1/16"; (INLET/2)+1.5"=24 1/32"; (INLET/2)+1.625"=24 3/32"; (INLET/2)-.125"=22 15/32"; (M-(B+.25")/2=3 31/32"; -(B+.25")/2=-29 1/32"; -P=-73"; A=41 3/4"; A+.25"=42"; A/2=20 7/8"; B=57 13/16"; B+.25"=58 1/16"; B/2=28 29/32"; BOTTOM=31 5/8"; C=3 7/16"; C+C=6 7/8"; C/2=1 23/32"; D=46 1/8"; D/2=23 1/16"; D/7=4 27/32"; E=62 1/16"; E/2=31 1/32"; F=67 9/16"; F-((D-A-.25")/2)=65 1/2"; G=35 15/16"; G+(INLET/2)+1.625"=60 1/32"; G-(INLET/2)-1.625"=11 27/32"; G-(R/2)=11 3/32"; H=75 1/2"; H-((D-A-.25")/2)=73 7/16"; H-J=44 3/4"; INLET=45 3/16"; INLET/2=22 19/32"; INLET/4=11 5/16"; J=30 3/4"; K=1 1/16"; K/2=17/32"; L=33"; M=66"; N=5 7/8"; P=73"; R=49 11/16"; R/2=24 27/32"; S=43"; S/2=21 1/2"; SCROLL2=24 27/32"; T=62 1/2"; T/2=31 1/4"; Type Comments=Centrifugal Airfoil Blower Clockwise Up Blast Arrangement 3 Low Profile Class 2; U=7"; U-N=1 1/8"; V=1 15/16"; V+(D-(A+.25"))/2=4"
- 445_CAF-DWDI_CW_UBD_CLASS_2: ((M+U+U+N+N)-((B+.25")/2))/2=5 3/32"; (A+.25")/2=23 3/32"; (B+.25")/2=32 1/4"; (D-(A+.25"))/2=2 1/16"; (INLET/2)+1.5"=26 5/32"; (INLET/2)+1.625"=26 7/32"; (INLET/2)-.125"=24 19/32"; (M-(B+.25")/2=3 31/32"; -(B+.25")/2=-32 1/4"; -P=-79 11/16"; A=45 15/16"; A+.25"=46 3/16"; A/2=22 31/32"; B=64 1/4"; B+.25"=64 1/2"; B/2=32 1/8"; BOTTOM=35"; C=2 7/16"; C+C=4 7/8"; C/2=1 7/32"; D=50 5/16"; D/2=25 5/32"; D/7=5 9/32"; E=68 9/16"; E/2=34 9/32"; F=74 11/16"; F-((D-A-.25")/2)=72 5/8"; G=39 11/16"; G+(INLET/2)+1.625"=65 29/32"; G-(INLET/2)-1.625"=13 15/32"; G-(R/2)=12 23/32"; H=83 5/16"; H-((D-A-.25")/2)=81 1/4"; H-J=49 1/4"; INLET=49 7/16"; INLET/2=24 23/32"; INLET/4=12 3/8"; J=34 1/16"; K=1 1/16"; K/2=17/32"; L=36 1/4"; M=72 7/16"; N=6 1/8"; P=79 11/16"; R=53 15/16"; R/2=26 31/32"; S=47 1/4"; S/2=23 5/8"; SCROLL2=26 31/32"; T=68 15/16"; T/2=34 15/32"; Type Comments=Centrifugal Airfoil Blower Clockwise Up Blast Arrangement 3 Low Profile Class 2; U=7 1/4"; U-N=1 1/8"; V=1 15/16"; V+(D-(A+.25"))/2=4"
- 490_CAF-DWDI_CW_UBD_CLASS_2: ((M+U+U+N+N)-((B+.25")/2))/2=5 3/32"; (A+.25")/2=25 5/8"; (B+.25")/2=35 3/16"; (D-(A+.25"))/2=2 3/32"; (INLET/2)+1.5"=28 15/16"; (INLET/2)+1.625"=29"; (INLET/2)-.125"=27 3/8"; (M-(B+.25")/2=4 31/32"; -(B+.25")/2=-35 3/16"; -P=-87 15/16"; A=51"; A+.25"=51 1/4"; A/2=25 1/2"; B=70 1/8"; B+.25"=70 3/8"; B/2=35 1/16"; BOTTOM=38 9/16"; C=2 15/16"; C+C=5 7/8"; C/2=1 15/32"; D=55 7/16"; D/2=27 23/32"; D/7=5 27/32"; E=74 7/16"; E/2=37 7/32"; F=82 1/8"; F-((D-A-.25")/2)=80 1/32"; G=43 9/16"; G+(INLET/2)+1.625"=72 9/16"; G-(INLET/2)-1.625"=14 9/16"; G-(R/2)=14 1/16"; H=91 1/2"; H-((D-A-.25")/2)=89 13/32"; H-J=54"; INLET=55"; INLET/2=27 1/2"; INLET/4=13 3/4"; J=37 1/2"; K=1 1/16"; K/2=17/32"; L=40 3/16"; M=80 5/16"; N=7 1/2"; P=87 15/16"; R=59"; R/2=29 1/2"; S=51"; S/2=25 1/2"; SCROLL2=29 11/32"; T=75 13/16"; T/2=37 29/32"; Type Comments=Centrifugal Airfoil Blower Clockwise Up Blast Arrangement 3 Low Profile Class 2; U=7 5/8"; U-N=1/8"; V=1 15/16"; V+(D-(A+.25"))/2=4 1/32"
- 540_CAF-DWDI_CW_UBD_CLASS_2: ((M+U+U+N+N)-((B+.25")/2))/2=6 5/8"; (A+.25")/2=28"; (B+.25")/2=39 3/32"; (D-(A+.25"))/2=2 9/16"; (INLET/2)+1.5"=31 7/16"; (INLET/2)+1.625"=31 1/2"; (INLET/2)-.125"=29 7/8"; (M-(B+.25")/2=5"; -(B+.25")/2=-39 3/32"; -P=-98 11/16"; A=55 3/4"; A+.25"=56"; A/2=27 7/8"; B=77 15/16"; B+.25"=78 3/16"; B/2=38 31/32"; BOTTOM=42 7/16"; C=3 7/16"; C+C=6 7/8"; C/2=1 23/32"; D=61 1/8"; D/2=30 9/16"; D/7=6 7/16"; E=83 1/8"; E/2=41 9/16"; F=90 3/8"; F-((D-A-.25")/2)=87 13/16"; G=47 15/16"; G+(INLET/2)+1.625"=79 7/16"; G-(INLET/2)-1.625"=16 7/16"; G-(R/2)=15 15/16"; H=101 3/16"; H-((D-A-.25")/2)=98 5/8"; H-J=59 7/8"; INLET=60"; INLET/2=30"; INLET/4=15"; J=41 5/16"; K=1 1/16"; K/2=17/32"; L=44 1/8"; M=88 3/16"; N=8 7/8"; P=98 11/16"; R=64"; R/2=32"; S=56"; S/2=28"; SCROLL2=31 27/32"; T=83 11/16"; T/2=41 27/32"; Type Comments=Centrifugal Airfoil Blower Clockwise Up Blast Arrangement 3 Low Profile Class 2; U=10 1/2"; U-N=1 5/8"; V=1 15/16"; V+(D-(A+.25"))/2=4 1/2"
- 600_CAF-DWDI_CW_UBD_CLASS_2: ((M+U+U+N+N)-((B+.25")/2))/2=6 5/8"; (A+.25")/2=31 7/32"; (B+.25")/2=43 1/4"; (D-(A+.25"))/2=2 9/16"; (INLET/2)+1.5"=34 7/16"; (INLET/2)+1.625"=34 1/2"; (INLET/2)-.125"=32 7/8"; (M-(B+.25")/2=6"; -(B+.25")/2=-43 1/4"; -P=-108"; A=62 3/16"; A+.25"=62 7/16"; A/2=31 3/32"; B=86 1/4"; B+.25"=86 1/2"; B/2=43 1/8"; BOTTOM=47 1/8"; C=3 7/16"; C+C=6 7/8"; C/2=1 23/32"; D=67 9/16"; D/2=33 25/32"; D/7=7 1/8"; E=91 7/16"; E/2=45 23/32"; F=100 5/16"; F-((D-A-.25")/2)=97 3/4"; G=53 3/16"; G+(INLET/2)+1.625"=87 11/16"; G-(INLET/2)-1.625"=18 11/16"; G-(R/2)=17 29/32"; H=112 1/8"; H-((D-A-.25")/2)=109 9/16"; H-J=66 3/16"; INLET=66"; INLET/2=33"; INLET/4=16 1/2"; J=45 15/16"; K=1 1/16"; K/2=17/32"; L=49 1/4"; M=98 1/2"; N=8 7/8"; P=108"; R=70 9/16"; R/2=35 9/32"; S=61"; S/2=30 1/2"; SCROLL2=35"; T=93"; T/2=46 1/2"; Type Comments=Centrifugal Airfoil Blower Clockwise Up Blast Arrangement 3 Low Profile Class 2; U=9 1/2"; U-N=5/8"; V=2 15/16"; V+(D-(A+.25"))/2=5 1/2"
- 660_CAF-DWDI_CW_UBD_CLASS_2: ((M+U+U+N+N)-((B+.25")/2))/2=6 5/8"; (A+.25")/2=34 11/32"; (B+.25")/2=47 9/16"; (D-(A+.25"))/2=2 9/16"; (INLET/2)+1.5"=37 7/16"; (INLET/2)+1.625"=37 1/2"; (INLET/2)-.125"=35 7/8"; (M-(B+.25")/2=6"; -(B+.25")/2=-47 9/16"; -P=-116 5/8"; A=68 7/16"; A+.25"=68 11/16"; A/2=34 7/32"; B=94 7/8"; B+.25"=95 1/8"; B/2=47 7/16"; BOTTOM=51 13/16"; C=3 7/16"; C+C=6 7/8"; C/2=1 23/32"; D=73 13/16"; D/2=36 29/32"; D/7=7 25/32"; E=100 1/4"; E/2=50 1/8"; F=110 3/16"; F-((D-A-.25")/2)=107 5/8"; G=58 3/8"; G+(INLET/2)+1.625"=95 7/8"; G-(INLET/2)-1.625"=20 7/8"; G-(R/2)=20 3/32"; H=123 1/16"; H-((D-A-.25")/2)=120 1/2"; H-J=72 9/16"; INLET=72"; INLET/2=36"; INLET/4=18"; J=50 1/2"; K=1 1/16"; K/2=17/32"; L=53 9/16"; M=107 1/8"; N=8 7/8"; P=116 5/8"; R=76 9/16"; R/2=38 9/32"; S=67"; S/2=33 1/2"; SCROLL2=38 9/32"; T=101 5/8"; T/2=50 13/16"; Type Comments=Centrifugal Airfoil Blower Clockwise Up Blast Arrangement 3 Low Profile Class 2; U=9 1/2"; U-N=5/8"; V=3 15/16"; V+(D-(A+.25"))/2=6 1/2"
- 730_CAF-DWDI_CW_UBD_CLASS_2: ((M+U+U+N+N)-((B+.25")/2))/2=6 11/16"; (A+.25")/2=38 1/32"; (B+.25")/2=52 1/2"; (D-(A+.25"))/2=2 5/8"; (INLET/2)+1.5"=40 15/16"; (INLET/2)+1.625"=41"; (INLET/2)-.125"=39 3/8"; (M-(B+.25")/2=6 1/16"; -(B+.25")/2=-52 1/2"; -P=-126 3/4"; A=75 13/16"; A+.25"=76 1/16"; A/2=37 29/32"; B=104 3/4"; B+.25"=105"; B/2=52 3/8"; BOTTOM=57 5/16"; C=3 15/16"; C+C=7 7/8"; C/2=1 31/32"; D=81 5/16"; D/2=40 21/32"; D/7=8 9/16"; E=110 1/8"; E/2=55 1/16"; F=121 13/16"; F-((D-A-.25")/2)=119 3/16"; G=64 1/2"; G+(INLET/2)+1.625"=105 1/2"; G-(INLET/2)-1.625"=23 1/2"; G-(R/2)=22 23/32"; H=135 7/8"; H-((D-A-.25")/2)=133 1/4"; H-J=80"; INLET=79"; INLET/2=39 1/2"; INLET/4=19 3/4"; J=55 7/8"; K=1 1/16"; K/2=17/32"; L=58 9/16"; M=117 1/8"; N=9"; P=126 3/4"; R=83 9/16"; R/2=41 25/32"; S=74"; S/2=37"; SCROLL2=41 25/32"; T=111 5/8"; T/2=55 13/16"; Type Comments=Centrifugal Airfoil Blower Clockwise Up Blast Arrangement 3 Low Profile Class 2; U=9 5/8"; U-N=5/8"; V=3 7/16"; V+(D-(A+.25"))/2=6 1/16"
- 120_CAF-DWDI_CW_UBD_CLASS_3: ((M+U+U+N+N)-((B+.25")/2))/2=4"; (A+.25")/2=6 3/16"; (B+.25")/2=8 31/32"; (D-(A+.25"))/2=15/16"; (INLET/2)+1.5"=9 1/2"; (INLET/2)+1.625"=9 9/16"; (INLET/2)-.125"=7 15/16"; (M-(B+.25")/2=2 15/16"; -(B+.25")/2=-8 31/32"; -P=-31 7/16"; A=12 1/8"; A+.25"=12 3/8"; A/2=6 1/16"; B=17 11/16"; B+.25"=17 15/16"; B/2=8 27/32"; BOTTOM=9 5/8"; C=1 11/16"; C+C=3 3/8"; C/2=27/32"; D=14 1/4"; D/2=7 1/8"; D/7=1 1/2"; E=19 13/16"; E/2=9 29/32"; F=21 1/16"; F-((D-A-.25")/2)=20 1/8"; G=11 7/16"; G+(INLET/2)+1.625"=21"; G-(INLET/2)-1.625"=1 7/8"; G-(R/2)=1 13/16"; H=23"; H-((D-A-.25")/2)=22 1/16"; H-J=13 3/4"; INLET=16 1/8"; INLET/2=8 1/16"; INLET/4=4 1/32"; J=9 1/4"; K=15/16"; K/2=15/32"; L=11 15/16"; M=23 13/16"; N=6 1/2"; P=31 7/16"; R=19 1/4"; R/2=9 5/8"; S=14 1/2"; S/2=7 1/4"; SCROLL2=9"; T=20 1/16"; T/2=10 1/32"; Type Comments=Centrifugal Airfoil Blower Clockwise Up Blast Arrangement 3 Low Profile Class 3; U=7 9/16"; U-N=1 1/16"; V=1"; V+(D-(A+.25"))/2=1 15/16"
- 135_CAF-DWDI_CW_UBD_CLASS_3: ((M+U+U+N+N)-((B+.25")/2))/2=4"; (A+.25")/2=6 15/16"; (B+.25")/2=10 3/32"; (D-(A+.25"))/2=15/16"; (INLET/2)+1.5"=10 1/4"; (INLET/2)+1.625"=10 5/16"; (INLET/2)-.125"=8 11/16"; (M-(B+.25")/2=2 15/16"; -(B+.25")/2=-10 3/32"; -P=-33 11/16"; A=13 5/8"; A+.25"=13 7/8"; A/2=6 13/16"; B=19 15/16"; B+.25"=20 3/16"; B/2=9 31/32"; BOTTOM=10 13/16"; C=1 15/16"; C+C=3 7/8"; C/2=31/32"; D=15 3/4"; D/2=7 7/8"; D/7=1 21/32"; E=22 1/16"; E/2=11 1/32"; F=23 9/16"; F-((D-A-.25")/2)=22 5/8"; G=12 3/4"; G+(INLET/2)+1.625"=23 1/16"; G-(INLET/2)-1.625"=2 7/16"; G-(R/2)=2 3/8"; H=25 3/4"; H-((D-A-.25")/2)=24 13/16"; H-J=15 3/8"; INLET=17 5/8"; INLET/2=8 13/16"; INLET/4=4 13/32"; J=10 3/8"; K=15/16"; K/2=15/32"; L=13 1/16"; M=26 1/16"; N=6 1/2"; P=33 11/16"; R=20 3/4"; R/2=10 3/8"; S=16 1/4"; S/2=8 1/8"; SCROLL2=10 1/2"; T=22 5/16"; T/2=11 5/32"; Type Comments=Centrifugal Airfoil Blower Clockwise Up Blast Arrangement 3 Low Profile Class 3; U=7 9/16"; U-N=1 1/16"; V=1"; V+(D-(A+.25"))/2=1 15/16"
- 150_CAF-DWDI_CW_UBD_CLASS_3: ((M+U+U+N+N)-((B+.25")/2))/2=4"; (A+.25")/2=7 3/4"; (B+.25")/2=11 1/8"; (D-(A+.25"))/2=15/16"; (INLET/2)+1.5"=11"; (INLET/2)+1.625"=11 1/16"; (INLET/2)-.125"=9 7/16"; (M-(B+.25")/2=2 15/16"; -(B+.25")/2=-11 1/8"; -P=-35 3/4"; A=15 1/4"; A+.25"=15 1/2"; A/2=7 5/8"; B=22"; B+.25"=22 1/4"; B/2=11"; BOTTOM=12"; C=1 15/16"; C+C=3 7/8"; C/2=31/32"; D=17 3/8"; D/2=8 11/16"; D/7=1 27/32"; E=24 1/8"; E/2=12 1/16"; F=26 1/16"; F-((D-A-.25")/2)=25 1/8"; G=14 1/16"; G+(INLET/2)+1.625"=25 1/8"; G-(INLET/2)-1.625"=3"; G-(R/2)=2 15/16"; H=28 7/16"; H-((D-A-.25")/2)=27 1/2"; H-J=16 15/16"; INLET=19 1/8"; INLET/2=9 9/16"; INLET/4=4 25/32"; J=11 1/2"; K=15/16"; K/2=15/32"; L=14 1/16"; M=28 1/8"; N=6 1/2"; P=35 3/4"; R=22 1/4"; R/2=11 1/8"; S=17 3/4"; S/2=8 7/8"; SCROLL2=11 1/4"; T=24 3/8"; T/2=12 3/16"; Type Comments=Centrifugal Airfoil Blower Clockwise Up Blast Arrangement 3 Low Profile Class 3; U=7 9/16"; U-N=1 1/16"; V=1"; V+(D-(A+.25"))/2=1 15/16"
- 165_CAF-DWDI_CW_UBD_CLASS_3: ((M+U+U+N+N)-((B+.25")/2))/2=4 1/2"; (A+.25")/2=8 19/32"; (B+.25")/2=12 1/8"; (D-(A+.25"))/2=15/16"; (INLET/2)+1.5"=12 1/32"; (INLET/2)+1.625"=12 3/32"; (INLET/2)-.125"=10 15/32"; (M-(B+.25")/2=2 15/16"; -(B+.25")/2=-12 1/8"; -P=-38 5/16"; A=16 15/16"; A+.25"=17 3/16"; A/2=8 15/32"; B=24"; B+.25"=24 1/4"; B/2=12"; BOTTOM=13 1/8"; C=2 3/16"; C+C=4 3/8"; C/2=1 3/32"; D=19 1/16"; D/2=9 17/32"; D/7=2"; E=26 1/8"; E/2=13 1/16"; F=28 1/2"; F-((D-A-.25")/2)=27 9/16"; G=15 3/8"; G+(INLET/2)+1.625"=27 15/32"; G-(INLET/2)-1.625"=3 9/32"; G-(R/2)=3 1/4"; H=31 3/16"; H-((D-A-.25")/2)=30 1/4"; H-J=18 1/2"; INLET=21 3/16"; INLET/2=10 19/32"; INLET/4=5 5/16"; J=12 11/16"; K=15/16"; K/2=15/32"; L=15 1/16"; M=30 1/8"; N=6 1/2"; P=38 5/16"; R=24 1/4"; R/2=12 1/8"; S=19 1/2"; S/2=9 3/4"; SCROLL2=12 1/8"; T=26 3/8"; T/2=13 3/16"; Type Comments=Centrifugal Airfoil Blower Clockwise Up Blast Arrangement 3 Low Profile Class 3; U=8 1/16"; U-N=1 9/16"; V=1"; V+(D-(A+.25"))/2=1 15/16"
- 180_CAF-DWDI_CW_UBD_CLASS_3: ((M+U+U+N+N)-((B+.25")/2))/2=4 1/2"; (A+.25")/2=9 3/8"; (B+.25")/2=13 5/32"; (D-(A+.25"))/2=15/16"; (INLET/2)+1.5"=12 25/32"; (INLET/2)+1.625"=12 27/32"; (INLET/2)-.125"=11 7/32"; (M-(B+.25")/2=2 15/16"; -(B+.25")/2=-13 5/32"; -P=-40 3/8"; A=18 1/2"; A+.25"=18 3/4"; A/2=9 1/4"; B=26 1/16"; B+.25"=26 5/16"; B/2=13 1/32"; BOTTOM=14 5/16"; C=2 3/16"; C+C=4 3/8"; C/2=1 3/32"; D=20 5/8"; D/2=10 5/16"; D/7=2 5/32"; E=28 3/16"; E/2=14 3/32"; F=31"; F-((D-A-.25")/2)=30 1/16"; G=16 11/16"; G+(INLET/2)+1.625"=29 17/32"; G-(INLET/2)-1.625"=3 27/32"; G-(R/2)=3 13/16"; H=33 15/16"; H-((D-A-.25")/2)=33"; H-J=20 1/8"; INLET=22 11/16"; INLET/2=11 11/32"; INLET/4=5 11/16"; J=13 13/16"; K=15/16"; K/2=15/32"; L=16 1/8"; M=32 3/16"; N=6 1/2"; P=40 3/8"; R=25 3/4"; R/2=12 7/8"; S=21"; S/2=10 1/2"; SCROLL2=13 3/8"; T=28 7/16"; T/2=14 7/32"; Type Comments=Centrifugal Airfoil Blower Clockwise Up Blast Arrangement 3 Low Profile Class 3; U=8 1/16"; U-N=1 9/16"; V=1"; V+(D-(A+.25"))/2=1 15/16"
- 195_CAF-DWDI_CW_UBD_CLASS_3: ((M+U+U+N+N)-((B+.25")/2))/2=4 1/2"; (A+.25")/2=9 7/8"; (B+.25")/2=14 11/32"; (D-(A+.25"))/2=1 15/16"; (INLET/2)+1.5"=13 17/32"; (INLET/2)+1.625"=13 19/32"; (INLET/2)-.125"=11 31/32"; (M-(B+.25")/2=2 15/16"; -(B+.25")/2=-14 11/32"; -P=-42 3/4"; A=19 1/2"; A+.25"=19 3/4"; A/2=9 3/4"; B=28 7/16"; B+.25"=28 11/16"; B/2=14 7/32"; BOTTOM=15 1/2"; C=2 3/16"; C+C=4 3/8"; C/2=1 3/32"; D=23 5/8"; D/2=11 13/16"; D/7=2 1/2"; E=32 9/16"; E/2=16 9/32"; F=33 1/2"; F-((D-A-.25")/2)=31 9/16"; G=18"; G+(INLET/2)+1.625"=31 19/32"; G-(INLET/2)-1.625"=4 13/32"; G-(R/2)=4 3/8"; H=37 11/16"; H-((D-A-.25")/2)=35 3/4"; H-J=22 3/4"; INLET=24 3/16"; INLET/2=12 3/32"; INLET/4=6 1/16"; J=14 15/16"; K=15/16"; K/2=15/32"; L=17 5/16"; M=34 9/16"; N=6 1/2"; P=42 3/4"; R=27 1/4"; R/2=13 5/8"; S=22 1/4"; S/2=11 1/8"; SCROLL2=14 1/4"; T=31 5/16"; T/2=15 21/32"; Type Comments=Centrifugal Airfoil Blower Clockwise Up Blast Arrangement 3 Low Profile Class 3; U=8 1/16"; U-N=1 9/16"; V=1"; V+(D-(A+.25"))/2=2 15/16"
- 210_CAF-DWDI_CW_UBD_CLASS_3: ((M+U+U+N+N)-((B+.25")/2))/2=4 1/2"; (A+.25")/2=10 15/16"; (B+.25")/2=15 5/16"; (D-(A+.25"))/2=1 15/16"; (INLET/2)+1.5"=14 13/32"; (INLET/2)+1.625"=14 15/32"; (INLET/2)-.125"=12 27/32"; (M-(B+.25")/2=2 15/16"; -(B+.25")/2=-15 5/16"; -P=-45 3/16"; A=21 5/8"; A+.25"=21 7/8"; A/2=10 13/16"; B=30 3/8"; B+.25"=30 5/8"; B/2=15 3/16"; BOTTOM=16 11/16"; C=2 3/16"; C+C=4 3/8"; C/2=1 3/32"; D=25 3/4"; D/2=12 7/8"; D/7=2 23/32"; E=34 1/2"; E/2=17 1/4"; F=36"; F-((D-A-.25")/2)=34 1/16"; G=19 5/16"; G+(INLET/2)+1.625"=33 25/32"; G-(INLET/2)-1.625"=4 27/32"; G-(R/2)=4 13/16"; H=40 3/8"; H-((D-A-.25")/2)=38 7/16"; H-J=24 1/4"; INLET=25 15/16"; INLET/2=12 31/32"; INLET/4=6 1/2"; J=16 1/8"; K=15/16"; K/2=15/32"; L=18 1/4"; M=36 1/2"; N=7"; P=45 3/16"; R=29"; R/2=14 1/2"; S=23 3/4"; S/2=11 7/8"; SCROLL2=15"; T=33 1/4"; T/2=16 5/8"; Type Comments=Centrifugal Airfoil Blower Clockwise Up Blast Arrangement 3 Low Profile Class 3; U=8 9/16"; U-N=1 9/16"; V=1"; V+(D-(A+.25"))/2=2 15/16"
- 225_CAF-DWDI_CW_UBD_CLASS_3: ((M+U+U+N+N)-((B+.25")/2))/2=4 1/2"; (A+.25")/2=11 23/32"; (B+.25")/2=16 3/8"; (D-(A+.25"))/2=2"; (INLET/2)+1.5"=15 5/32"; (INLET/2)+1.625"=15 7/32"; (INLET/2)-.125"=13 19/32"; (M-(B+.25")/2=2 15/16"; -(B+.25")/2=-16 3/8"; -P=-47 5/16"; A=23 3/16"; A+.25"=23 7/16"; A/2=11 19/32"; B=32 1/2"; B+.25"=32 3/4"; B/2=16 1/4"; BOTTOM=17 13/16"; C=2 3/16"; C+C=4 3/8"; C/2=1 3/32"; D=27 7/16"; D/2=13 23/32"; D/7=2 7/8"; E=36 11/16"; E/2=18 11/32"; F=38 3/8"; F-((D-A-.25")/2)=36 3/8"; G=20 9/16"; G+(INLET/2)+1.625"=35 25/32"; G-(INLET/2)-1.625"=5 11/32"; G-(R/2)=5 5/16"; H=43 3/16"; H-((D-A-.25")/2)=41 3/16"; H-J=25 15/16"; INLET=27 7/16"; INLET/2=13 23/32"; INLET/4=6 7/8"; J=17 1/4"; K=15/16"; K/2=15/32"; L=19 5/16"; M=38 5/8"; N=7"; P=47 5/16"; R=30 1/2"; R/2=15 1/4"; S=25 1/2"; S/2=12 3/4"; SCROLL2=15 7/8"; T=35 3/8"; T/2=17 11/16"; Type Comments=Centrifugal Airfoil Blower Clockwise Up Blast Arrangement 3 Low Profile Class 3; U=8 9/16"; U-N=1 9/16"; V=1"; V+(D-(A+.25"))/2=3"
- 245_CAF-DWDI_CW_UBD_CLASS_3: ((M+U+U+N+N)-((B+.25")/2))/2=4 1/2"; (A+.25")/2=12 7/8"; (B+.25")/2=17 21/32"; (D-(A+.25"))/2=2"; (INLET/2)+1.5"=16 5/32"; (INLET/2)+1.625"=16 7/32"; (INLET/2)-.125"=14 19/32"; (M-(B+.25")/2=3 15/16"; -(B+.25")/2=-17 21/32"; -P=-50 13/16"; A=25 1/2"; A+.25"=25 3/4"; A/2=12 3/4"; B=35 1/16"; B+.25"=35 5/16"; B/2=17 17/32"; BOTTOM=19 3/8"; C=2 7/16"; C+C=4 7/8"; C/2=1 7/32"; D=29 3/4"; D/2=14 7/8"; D/7=3 1/8"; E=39 1/4"; E/2=19 5/8"; F=41 11/16"; F-((D-A-.25")/2)=39 11/16"; G=22 5/16"; G+(INLET/2)+1.625"=38 17/32"; G-(INLET/2)-1.625"=6 3/32"; G-(R/2)=5 27/32"; H=46 13/16"; H-((D-A-.25")/2)=44 13/16"; H-J=28 1/16"; INLET=29 7/16"; INLET/2=14 23/32"; INLET/4=7 3/8"; J=18 3/4"; K=1 1/16"; K/2=17/32"; L=21 5/8"; M=43 3/16"; N=7"; P=50 13/16"; R=32 15/16"; R/2=16 15/32"; S=27 1/8"; S/2=13 9/16"; SCROLL2=16 7/8"; T=38 9/16"; T/2=19 9/32"; Type Comments=Centrifugal Airfoil Blower Clockwise Up Blast Arrangement 3 Low Profile Class 3; U=7 9/16"; U-N=9/16"; V=1"; V+(D-(A+.25"))/2=3"
- 270_CAF-DWDI_CW_UBD_CLASS_3: ((M+U+U+N+N)-((B+.25")/2))/2=4 1/2"; (A+.25")/2=13 7/8"; (B+.25")/2=19 27/32"; (D-(A+.25"))/2=2"; (INLET/2)+1.5"=17 13/32"; (INLET/2)+1.625"=17 15/32"; (INLET/2)-.125"=15 27/32"; (M-(B+.25")/2=3 15/16"; -(B+.25")/2=-19 27/32"; -P=-55 5/16"; A=27 1/2"; A+.25"=27 3/4"; A/2=13 3/4"; B=39 7/16"; B+.25"=39 11/16"; B/2=19 23/32"; BOTTOM=21 5/16"; C=2 7/16"; C+C=4 7/8"; C/2=1 7/32"; D=31 3/4"; D/2=15 7/8"; D/7=3 11/32"; E=43 5/8"; E/2=21 13/16"; F=45 13/16"; F-((D-A-.25")/2)=43 13/16"; G=24 1/2"; G+(INLET/2)+1.625"=41 31/32"; G-(INLET/2)-1.625"=7 1/32"; G-(R/2)=6 21/32"; H=51 3/8"; H-((D-A-.25")/2)=49 3/8"; H-J=30 11/16"; INLET=31 15/16"; INLET/2=15 31/32"; INLET/4=8"; J=20 11/16"; K=1 1/16"; K/2=17/32"; L=23 13/16"; M=47 9/16"; N=7 1/8"; P=55 5/16"; R=35 11/16"; R/2=17 27/32"; S=29 7/8"; S/2=14 15/16"; SCROLL2=18 3/4"; T=42 15/16"; T/2=21 15/32"; Type Comments=Centrifugal Airfoil Blower Clockwise Up Blast Arrangement 3 Low Profile Class 3; U=7 11/16"; U-N=9/16"; V=1"; V+(D-(A+.25"))/2=3"
- 300_CAF-DWDI_CW_UBD_CLASS_3: ((M+U+U+N+N)-((B+.25")/2))/2=4 9/16"; (A+.25")/2=15 23/32"; (B+.25")/2=21 5/8"; (D-(A+.25"))/2=2"; (INLET/2)+1.5"=18 29/32"; (INLET/2)+1.625"=18 31/32"; (INLET/2)-.125"=17 11/32"; (M-(B+.25")/2=3 15/16"; -(B+.25")/2=-21 5/8"; -P=-58 7/8"; A=31 3/16"; A+.25"=31 7/16"; A/2=15 19/32"; B=43"; B+.25"=43 1/4"; B/2=21 1/2"; BOTTOM=23 11/16"; C=2 7/16"; C+C=4 7/8"; C/2=1 7/32"; D=35 7/16"; D/2=17 23/32"; D/7=3 23/32"; E=47 3/16"; E/2=23 19/32"; F=50 3/4"; F-((D-A-.25")/2)=48 3/4"; G=27 1/16"; G+(INLET/2)+1.625"=46 1/32"; G-(INLET/2)-1.625"=8 3/32"; G-(R/2)=7 23/32"; H=56 7/8"; H-((D-A-.25")/2)=54 7/8"; H-J=33 15/16"; INLET=34 15/16"; INLET/2=17 15/32"; INLET/4=8 3/4"; J=22 15/16"; K=1 1/16"; K/2=17/32"; L=25 9/16"; M=51 1/8"; N=7 1/8"; P=58 7/8"; R=38 11/16"; R/2=19 11/32"; S=32 7/8"; S/2=16 7/16"; SCROLL2=20 1/4"; T=46 1/2"; T/2=23 1/4"; Type Comments=Centrifugal Airfoil Blower Clockwise Up Blast Arrangement 3 Low Profile Class 3; U=7 3/4"; U-N=5/8"; V=1"; V+(D-(A+.25"))/2=3"
- 330_CAF-DWDI_CW_UBD_CLASS_3: ((M+U+U+N+N)-((B+.25")/2))/2=4 19/32"; (A+.25")/2=17 3/8"; (B+.25")/2=23 21/32"; (D-(A+.25"))/2=2 1/16"; (INLET/2)+1.5"=20 13/32"; (INLET/2)+1.625"=20 15/32"; (INLET/2)-.125"=18 27/32"; (M-(B+.25")/2=4 31/32"; -(B+.25")/2=-23 21/32"; -P=-64"; A=34 1/2"; A+.25"=34 3/4"; A/2=17 1/4"; B=47 1/16"; B+.25"=47 5/16"; B/2=23 17/32"; BOTTOM=26 1/16"; C=2 7/16"; C+C=4 7/8"; C/2=1 7/32"; D=38 7/8"; D/2=19 7/16"; D/7=4 3/32"; E=51 5/16"; E/2=25 21/32"; F=55 3/4"; F-((D-A-.25")/2)=53 11/16"; G=29 11/16"; G+(INLET/2)+1.625"=50 5/32"; G-(INLET/2)-1.625"=9 7/32"; G-(R/2)=8 9/16"; H=62 3/8"; H-((D-A-.25")/2)=60 5/16"; H-J=37 1/16"; INLET=37 15/16"; INLET/2=18 31/32"; INLET/4=9 1/2"; J=25 5/16"; K=1 1/16"; K/2=17/32"; L=28 5/8"; M=57 1/4"; N=7 1/8"; P=64"; R=42 1/4"; R/2=21 1/8"; S=35 1/4"; S/2=17 5/8"; SCROLL2=20 25/32"; T=51 3/4"; T/2=25 7/8"; Type Comments=Centrifugal Airfoil Blower Clockwise Up Blast Arrangement 3 Low Profile Class 3; U=6 3/4"; U-N=-3/8"; V=1"; V+(D-(A+.25"))/2=3 1/16"
- 365_CAF-DWDI_CW_UBD_CLASS_3: ((M+U+U+N+N)-((B+.25")/2))/2=5 3/32"; (A+.25")/2=19 15/32"; (B+.25")/2=26 7/32"; (D-(A+.25"))/2=2 9/16"; (INLET/2)+1.5"=22 5/32"; (INLET/2)+1.625"=22 7/32"; (INLET/2)-.125"=20 19/32"; (M-(B+.25")/2=4 31/32"; -(B+.25")/2=-26 7/32"; -P=-70 1/8"; A=38 11/16"; A+.25"=38 15/16"; A/2=19 11/32"; B=52 3/16"; B+.25"=52 7/16"; B/2=26 3/32"; BOTTOM=28 3/4"; C=2 15/16"; C+C=5 7/8"; C/2=1 15/32"; D=44 1/16"; D/2=22 1/32"; D/7=4 5/8"; E=57 7/16"; E/2=28 23/32"; F=61 1/2"; F-((D-A-.25")/2)=58 15/16"; G=32 3/4"; G+(INLET/2)+1.625"=54 31/32"; G-(INLET/2)-1.625"=10 17/32"; G-(R/2)=9 3/4"; H=69 1/4"; H-((D-A-.25")/2)=66 11/16"; H-J=41 5/16"; INLET=41 7/16"; INLET/2=20 23/32"; INLET/4=10 3/8"; J=27 15/16"; K=1 1/16"; K/2=17/32"; L=31 3/16"; M=62 3/8"; N=7 5/8"; P=70 1/8"; R=46"; R/2=23"; S=39"; S/2=19 1/2"; SCROLL2=22 21/32"; T=56 7/8"; T/2=28 7/16"; Type Comments=Centrifugal Airfoil Blower Clockwise Up Blast Arrangement 3 Low Profile Class 3; U=7 3/4"; U-N=1/8"; V=1"; V+(D-(A+.25"))/2=3 9/16"
- 402_CAF-DWDI_CW_UBD_CLASS_3: ((M+U+U+N+N)-((B+.25")/2))/2=6 19/32"; (A+.25")/2=21"; (B+.25")/2=29 1/32"; (D-(A+.25"))/2=2 9/16"; (INLET/2)+1.5"=24 1/32"; (INLET/2)+1.625"=24 3/32"; (INLET/2)-.125"=22 15/32"; (M-(B+.25")/2=5 31/32"; -(B+.25")/2=-29 1/32"; -P=-80 3/4"; A=41 3/4"; A+.25"=42"; A/2=20 7/8"; B=57 13/16"; B+.25"=58 1/16"; B/2=28 29/32"; BOTTOM=31 5/8"; C=3 7/16"; C+C=6 7/8"; C/2=1 23/32"; D=47 1/8"; D/2=23 9/16"; D/7=4 31/32"; E=63 1/16"; E/2=31 17/32"; F=67 9/16"; F-((D-A-.25")/2)=65"; G=35 15/16"; G+(INLET/2)+1.625"=60 1/32"; G-(INLET/2)-1.625"=11 27/32"; G-(R/2)=10 21/32"; H=76"; H-((D-A-.25")/2)=73 7/16"; H-J=45 1/4"; INLET=45 3/16"; INLET/2=22 19/32"; INLET/4=11 5/16"; J=30 3/4"; K=1 1/16"; K/2=17/32"; L=35"; M=70"; N=10 1/8"; P=80 3/4"; R=50 9/16"; R/2=25 9/32"; S=42"; S/2=21"; SCROLL2=24 27/32"; T=63 1/2"; T/2=31 3/4"; Type Comments=Centrifugal Airfoil Blower Clockwise Up Blast Arrangement 3 Low Profile Class 3; U=10 3/4"; U-N=5/8"; V=1 15/16"; V+(D-(A+.25"))/2=4 1/2"
- 445_CAF-DWDI_CW_UBD_CLASS_3: ((M+U+U+N+N)-((B+.25")/2))/2=6 5/8"; (A+.25")/2=23 3/32"; (B+.25")/2=32 1/4"; (D-(A+.25"))/2=2 9/16"; (INLET/2)+1.5"=26 5/32"; (INLET/2)+1.625"=26 7/32"; (INLET/2)-.125"=24 19/32"; (M-(B+.25")/2=6"; -(B+.25")/2=-32 1/4"; -P=-87 1/4"; A=45 15/16"; A+.25"=46 3/16"; A/2=22 31/32"; B=64 1/4"; B+.25"=64 1/2"; B/2=32 1/8"; BOTTOM=35"; C=3 7/16"; C+C=6 7/8"; C/2=1 23/32"; D=51 5/16"; D/2=25 21/32"; D/7=5 13/32"; E=69 9/16"; E/2=34 25/32"; F=74 11/16"; F-((D-A-.25")/2)=72 1/8"; G=39 11/16"; G+(INLET/2)+1.625"=65 29/32"; G-(INLET/2)-1.625"=13 15/32"; G-(R/2)=12 9/32"; H=83 7/8"; H-((D-A-.25")/2)=81 5/16"; H-J=49 13/16"; INLET=49 7/16"; INLET/2=24 23/32"; INLET/4=12 3/8"; J=34 1/16"; K=1 1/16"; K/2=17/32"; L=38 1/4"; M=76 1/2"; N=10 1/8"; P=87 1/4"; R=54 13/16"; R/2=27 13/32"; S=46 1/4"; S/2=23 1/8"; SCROLL2=26 31/32"; T=70"; T/2=35"; Type Comments=Centrifugal Airfoil Blower Clockwise Up Blast Arrangement 3 Low Profile Class 3; U=10 3/4"; U-N=5/8"; V=1 15/16"; V+(D-(A+.25"))/2=4 1/2"
- 490_CAF-DWDI_CW_UBD_CLASS_3: ((M+U+U+N+N)-((B+.25")/2))/2=6 5/8"; (A+.25")/2=25 5/8"; (B+.25")/2=35 3/16"; (D-(A+.25"))/2=2 9/16"; (INLET/2)+1.5"=28 15/16"; (INLET/2)+1.625"=29"; (INLET/2)-.125"=27 3/8"; (M-(B+.25")/2=8"; -(B+.25")/2=-35 3/16"; -P=-98 1/2"; A=51"; A+.25"=51 1/4"; A/2=25 1/2"; B=70 1/8"; B+.25"=70 3/8"; B/2=35 1/16"; BOTTOM=38 9/16"; C=3 15/16"; C+C=7 7/8"; C/2=1 31/32"; D=56 3/8"; D/2=28 3/16"; D/7=5 15/16"; E=75 7/16"; E/2=37 23/32"; F=82 3/16"; F-((D-A-.25")/2)=79 5/8"; G=43 5/8"; G+(INLET/2)+1.625"=72 5/8"; G-(INLET/2)-1.625"=14 5/8"; G-(R/2)=13 5/8"; H=92 1/16"; H-((D-A-.25")/2)=89 1/2"; H-J=54 9/16"; INLET=55"; INLET/2=27 1/2"; INLET/4=13 3/4"; J=37 1/2"; K=1 1/16"; K/2=17/32"; L=43 3/16"; M=86 3/8"; N=13 1/2"; P=98 1/2"; R=60"; R/2=30"; S=50"; S/2=25"; SCROLL2=29 11/32"; T=76 7/8"; T/2=38 7/16"; Type Comments=Centrifugal Airfoil Blower Clockwise Up Blast Arrangement 3 Low Profile Class 3; U=12 1/8"; U-N=-1 3/8"; V=1 15/16"; V+(D-(A+.25"))/2=4 1/2"
- 540_CAF-DWDI_CW_UBD_CLASS_3: ((M+U+U+N+N)-((B+.25")/2))/2=8 11/16"; (A+.25")/2=28"; (B+.25")/2=39 3/32"; (D-(A+.25"))/2=2 5/8"; (INLET/2)+1.5"=31 7/16"; (INLET/2)+1.625"=31 1/2"; (INLET/2)-.125"=29 7/8"; (M-(B+.25")/2=8 1/16"; -(B+.25")/2=-39 3/32"; -P=-110 11/16"; A=55 3/4"; A+.25"=56"; A/2=27 7/8"; B=77 15/16"; B+.25"=78 3/16"; B/2=38 31/32"; BOTTOM=42 7/16"; C=4 7/16"; C+C=8 7/8"; C/2=2 7/32"; D=61 1/4"; D/2=30 5/8"; D/7=6 7/16"; E=83 3/8"; E/2=41 11/16"; F=90 7/16"; F-((D-A-.25")/2)=87 13/16"; G=48"; G+(INLET/2)+1.625"=79 1/2"; G-(INLET/2)-1.625"=16 1/2"; G-(R/2)=15 1/2"; H=101 1/4"; H-((D-A-.25")/2)=98 5/8"; H-J=59 7/8"; INLET=60"; INLET/2=30"; INLET/4=15"; J=41 3/8"; K=1 3/16"; K/2=19/32"; L=47 1/8"; M=94 5/16"; N=15 3/4"; P=110 11/16"; R=65"; R/2=32 1/2"; S=55"; S/2=27 1/2"; SCROLL2=31 27/32"; T=84 13/16"; T/2=42 13/32"; Type Comments=Centrifugal Airfoil Blower Clockwise Up Blast Arrangement 3 Low Profile Class 3; U=16 3/8"; U-N=5/8"; V=1 15/16"; V+(D-(A+.25"))/2=4 9/16"
- 600_CAF-DWDI_CW_UBD_CLASS_3: ((M+U+U+N+N)-((B+.25")/2))/2=8 3/16"; (A+.25")/2=31 7/32"; (B+.25")/2=43 1/4"; (D-(A+.25"))/2=2 21/32"; (INLET/2)+1.5"=34 7/16"; (INLET/2)+1.625"=34 1/2"; (INLET/2)-.125"=32 7/8"; (M-(B+.25")/2=8 1/16"; -(B+.25")/2=-43 1/4"; -P=-118 5/8"; A=62 3/16"; A+.25"=62 7/16"; A/2=31 3/32"; B=86 1/4"; B+.25"=86 1/2"; B/2=43 1/8"; BOTTOM=47 1/8"; C=4 15/16"; C+C=9 7/8"; C/2=2 15/32"; D=67 3/4"; D/2=33 7/8"; D/7=7 1/8"; E=91 11/16"; E/2=45 27/32"; F=100 5/16"; F-((D-A-.25")/2)=97 21/32"; G=53 3/16"; G+(INLET/2)+1.625"=87 11/16"; G-(INLET/2)-1.625"=18 11/16"; G-(R/2)=17 11/16"; H=112 3/16"; H-((D-A-.25")/2)=109 17/32"; H-J=66 1/4"; INLET=66"; INLET/2=33"; INLET/4=16 1/2"; J=45 15/16"; K=1 3/16"; K/2=19/32"; L=51 5/16"; M=102 5/8"; N=15 7/8"; P=118 5/8"; R=71"; R/2=35 1/2"; S=61"; S/2=30 1/2"; SCROLL2=35"; T=93 1/8"; T/2=46 9/16"; Type Comments=Centrifugal Airfoil Blower Clockwise Up Blast Arrangement 3 Low Profile Class 3; U=16"; U-N=1/8"; V=2 15/16"; V+(D-(A+.25"))/2=5 19/32"

## geometry (parser evidence)
native form markers: Sweep x3
no freeform markers — native parametric forms only
